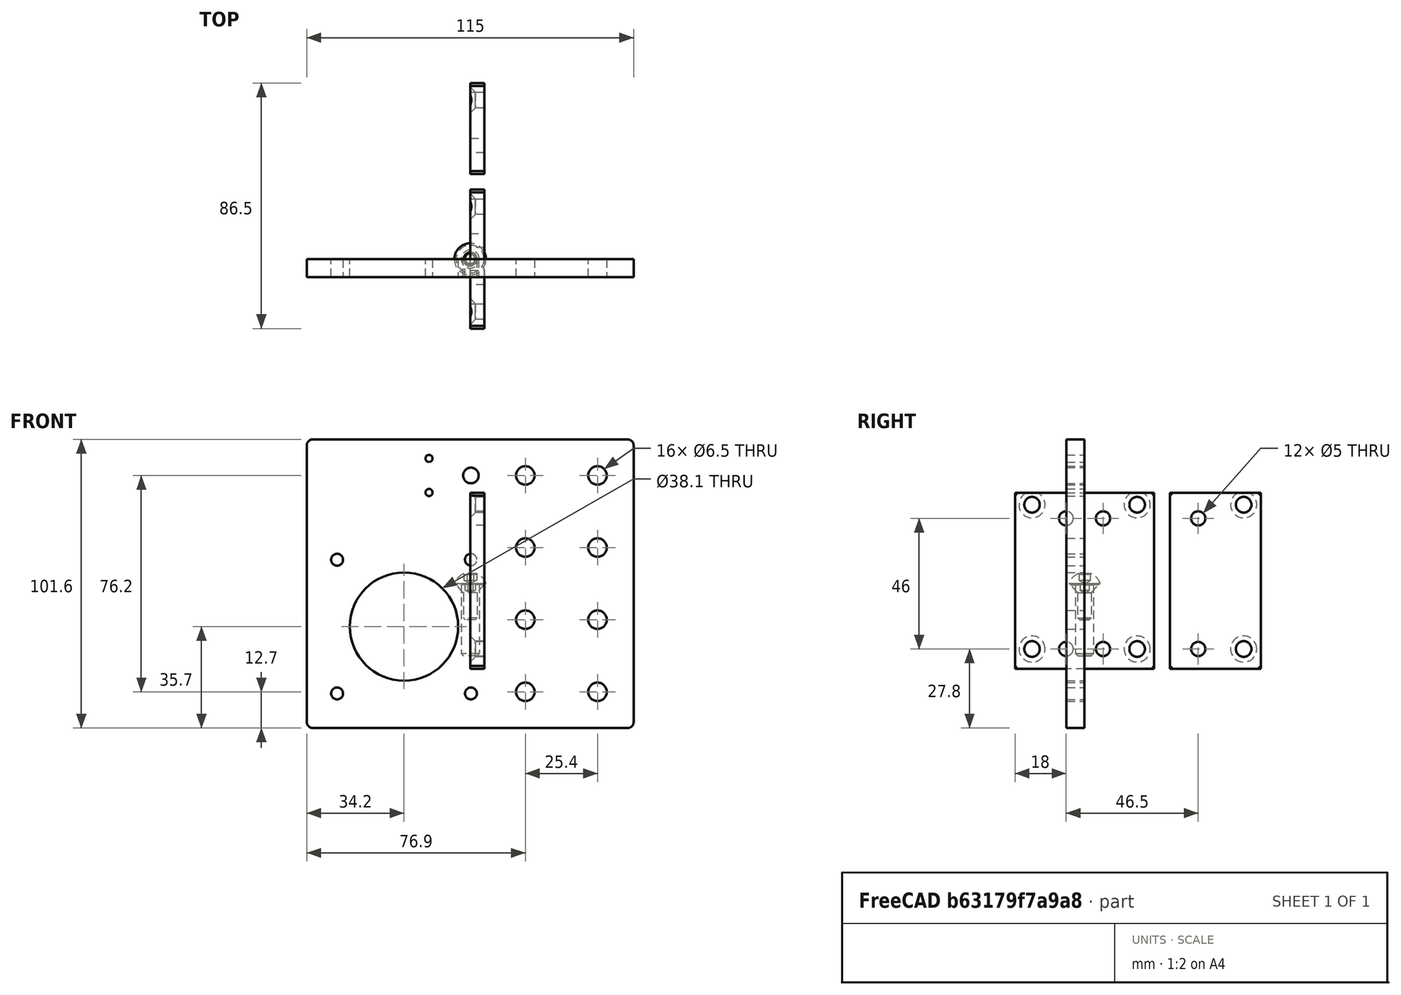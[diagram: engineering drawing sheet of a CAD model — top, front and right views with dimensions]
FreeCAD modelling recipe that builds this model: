
FCSTD DOCUMENT  (FreeCAD 2021.717R24301 +3842 (Git))
Label: Y axis plates
License: Creative Commons Attribution
LicenseURL: http://creativecommons.org/licenses/by/4.0/
objects: App::FeaturePython×164, Part::FeaturePython×120, TechDraw::DrawViewDimension×48, App::LinkElement×44, App::Link×16, PartDesign::Body×8, Sketcher::SketchObject×5, TechDraw::DrawViewPart×5, PartDesign::Pad×4, PartDesign::SubShapeBinder×4, PartDesign::Chamfer×4, PartDesign::Hole×4, TechDraw::DrawSVGTemplate×3, App::DocumentObjectGroup×3, TechDraw::DrawPage×3, PartDesign::Fillet×2, PartDesign::ShapeBinder×1, PartDesign::Pocket×1, TechDraw::DrawViewAnnotation×1
note: 175 computed .brp shape members not serialized (recipe doc carries the construction recipe); baked Part::Feature solids carry a one-line shape summary decoded from their .brp

FEATURE [Sketcher::SketchObject] Sketch
  FullyConstrained = true
  MapMode = 5
  Placement = pos=(0,0,0) rot=(0.57735,0.57735,0.57735;2.0944rad)
  Support = -> [YZ_Plane]
  sketch-geometry (16):
    g0: LineSegment StartX=-24.5 StartY=32 StartZ=0 EndX=24.5 EndY=32 EndZ=0
    g1: LineSegment StartX=24.5 StartY=32 StartZ=0 EndX=24.5 EndY=-30 EndZ=0
    g2: LineSegment StartX=24.5 StartY=-30 StartZ=0 EndX=-24.5 EndY=-30 EndZ=0
    g3: LineSegment StartX=-24.5 StartY=-30 StartZ=0 EndX=-24.5 EndY=32 EndZ=0
    g4: LineSegment [constr] StartX=-12.5 StartY=30 StartZ=0 EndX=12.5 EndY=30 EndZ=0
    g5: LineSegment [constr] StartX=12.5 StartY=30 StartZ=0 EndX=12.5 EndY=-30 EndZ=0
    g6: LineSegment [constr] StartX=12.5 StartY=-30 StartZ=0 EndX=-12.5 EndY=-30 EndZ=0
    g7: LineSegment [constr] StartX=-12.5 StartY=-30 StartZ=0 EndX=-12.5 EndY=30 EndZ=0
    g8: Circle CenterX=-6.5 CenterY=23 CenterZ=0 NormalX=0 NormalY=0 NormalZ=1 AngleXU=0 Radius=2.5
    g9: Circle CenterX=6.5 CenterY=23 CenterZ=0 NormalX=0 NormalY=0 NormalZ=1 AngleXU=0 Radius=2.5
    g10: Circle CenterX=-6.5 CenterY=-23 CenterZ=0 NormalX=0 NormalY=0 NormalZ=1 AngleXU=0 Radius=2.5
    g11: Circle CenterX=6.5 CenterY=-23 CenterZ=0 NormalX=0 NormalY=0 NormalZ=1 AngleXU=0 Radius=2.5
    g12: Circle CenterX=18.5 CenterY=-23 CenterZ=0 NormalX=0 NormalY=0 NormalZ=1 AngleXU=0 Radius=2.75
    g13: Circle CenterX=18.5 CenterY=27.8 CenterZ=0 NormalX=0 NormalY=0 NormalZ=1 AngleXU=0 Radius=2.75
    g14: Circle CenterX=-18.5 CenterY=27.8 CenterZ=0 NormalX=0 NormalY=0 NormalZ=1 AngleXU=0 Radius=2.75
    g15: Circle CenterX=-18.5 CenterY=-23 CenterZ=0 NormalX=0 NormalY=0 NormalZ=1 AngleXU=0 Radius=2.75
  constraints (44):
    c: Coincident(g0,g1)
    c: Coincident(g1,g2)
    c: Coincident(g2,g3)
    c: Coincident(g3,g0)
    c: Horizontal(g0)
    c: Vertical(g1)
    c: Vertical(g3)
    c: Coincident(g4,g5)
    c: Coincident(g5,g6)
    c: Coincident(g6,g7)
    c: Coincident(g7,g4)
    c: Horizontal(g4)
    c: Horizontal(g6)
    c: Vertical(g5)
    c: Vertical(g7)
    c: Symmetric(g5,g4,g-1)
    c: DistanceY(g5,g5) = 60
    c: DistanceX(g4,g4) = 25
    c: Symmetric(g8,g11,g-1)
    c: Vertical(g8,g10)
    c: Vertical(g9,g11)
    c: Horizontal(g8,g9)
    c: Horizontal(g10,g11)
    c: Equal(g8,g9)
    c: Diameter(g9) = 5
    c: DistanceX(g10,g11) = 13
    c: DistanceY(g11,g9) = 46
    c: Horizontal(g2,g6)
    c: DistanceX(g4,g13) = 6
    c: DistanceX(g13,g0) = 6
    c: DistanceY(g12,g13) = 50.8
    c: Equal(g13,g12)
    c: Diameter(g13) = 5.5
    c: Vertical(g12,g13)
    c: Horizontal(g11,g12)
    c: Symmetric(g1,g2,g-2)
    c: Equal(g15,g14)
    c: Equal(g14,g13)
    c: Horizontal(g14,g13)
    c: Symmetric(g12,g15,g-2)
    c: Vertical(g14,g15)
    c: Equal(g10,g11)
    c: Equal(g10,g8)
    c: DistanceY(g3,g3) = 62
FEATURE [PartDesign::Pad] Pad
  ClaimChildren = false
  Direction = (1,1,1)
  Fit = 0
  FitJoin = 0
  InnerFit = 0
  InnerFitJoin = 0
  InnerTaperAngle = 0
  InnerTaperAngleRev = 0
  Length = 5
  Length2 = 100
  Linearize = true
  NewSolid = false
  Placement = pos=(0,0,0) rot=(0.57735,0.57735,0.57735;2.0944rad)
  Profile = -> Sketch
  Refine = true
  Suppress = false
  Type = 0
  _ProfileBasedVersion = 0
FEATURE [PartDesign::Body] Body  label="BK12 plate"
  AutoGroupSolids = false
  ExportMode = 0
  Group = -> [Sketch,Pad]
  Origin = -> Origin
  Tip = -> Pad
  _ExportChildren = -> [Pad]
  _GroupVersion = 1
FEATURE [Sketcher::SketchObject] Sketch001
  FullyConstrained = true
  MapMode = 5
  Placement = pos=(0,0,0) rot=(0.57735,0.57735,0.57735;2.0944rad)
  Support = -> [YZ_Plane001]
  sketch-geometry (12):
    g0: LineSegment [constr] StartX=-10 StartY=30 StartZ=0 EndX=10 EndY=30 EndZ=0
    g1: LineSegment [constr] StartX=10 StartY=30 StartZ=0 EndX=10 EndY=-30 EndZ=0
    g2: LineSegment [constr] StartX=10 StartY=-30 StartZ=0 EndX=-10 EndY=-30 EndZ=0
    g3: LineSegment [constr] StartX=-10 StartY=-30 StartZ=0 EndX=-10 EndY=30 EndZ=0
    g4: Circle CenterX=0 CenterY=23 CenterZ=0 NormalX=0 NormalY=0 NormalZ=1 AngleXU=0 Radius=2.5
    g5: Circle CenterX=0 CenterY=-23 CenterZ=0 NormalX=0 NormalY=0 NormalZ=1 AngleXU=0 Radius=2.5
    g6: Circle CenterX=16 CenterY=27.8 CenterZ=0 NormalX=0 NormalY=0 NormalZ=1 AngleXU=0 Radius=2.75
    g7: Circle CenterX=16 CenterY=-23 CenterZ=0 NormalX=0 NormalY=0 NormalZ=1 AngleXU=0 Radius=2.75
    g8: LineSegment StartX=-10 StartY=-30 StartZ=0 EndX=22 EndY=-30 EndZ=0
    g9: LineSegment StartX=22 StartY=-30 StartZ=0 EndX=22 EndY=32 EndZ=0
    g10: LineSegment StartX=22 StartY=32 StartZ=0 EndX=-10 EndY=32 EndZ=0
    g11: LineSegment StartX=-10 StartY=32 StartZ=0 EndX=-10 EndY=-30 EndZ=0
  constraints (33):
    c: Coincident(g0,g1)
    c: Coincident(g1,g2)
    c: Coincident(g2,g3)
    c: Coincident(g3,g0)
    c: Horizontal(g0)
    c: Horizontal(g2)
    c: Vertical(g1)
    c: Vertical(g3)
    c: Symmetric(g1,g0,g-1)
    c: DistanceX(g0,g0) = 20
    c: DistanceY(g1,g1) = 60
    c: PointOnObject(g4,g-2)
    c: Symmetric(g5,g4,g-1)
    c: DistanceY(g5,g4) = 46
    c: Diameter(g4) = 5
    c: Diameter(g7) = 5.5
    c: Equal(g7,g6)
    c: Horizontal(g7,g5)
    c: Vertical(g7,g6)
    c: DistanceY(g7,g6) = 50.8
    c: DistanceX(g0,g6) = 6
    c: Coincident(g8,g9)
    c: Coincident(g9,g10)
    c: Coincident(g10,g11)
    c: Coincident(g11,g8)
    c: Horizontal(g8)
    c: Horizontal(g10)
    c: Vertical(g9)
    c: Vertical(g11)
    c: Coincident(g8,g2)
    c: DistanceX(g6,g9) = 6
    c: Equal(g5,g4)
    c: DistanceY(g9,g9) = 62
FEATURE [PartDesign::Pad] Pad001
  ClaimChildren = false
  Direction = (1,1,1)
  Fit = 0
  FitJoin = 0
  InnerFit = 0
  InnerFitJoin = 0
  InnerTaperAngle = 0
  InnerTaperAngleRev = 0
  Length = 5
  Length2 = 100
  Linearize = true
  NewSolid = false
  Placement = pos=(0,0,0) rot=(0.57735,0.57735,0.57735;2.0944rad)
  Profile = -> Sketch001
  Refine = true
  Suppress = false
  Type = 0
  _ProfileBasedVersion = 0
FEATURE [PartDesign::Body] Body001  label="BF12 plate"
  AutoGroupSolids = false
  ExportMode = 0
  Group = -> [Sketch001,Pad001]
  Origin = -> Origin001
  Placement = pos=(0,40,0) rot=(0,0,1;0rad)
  Tip = -> Pad001
  _ExportChildren = -> [Pad001]
  _GroupVersion = 1
FEATURE [PartDesign::SubShapeBinder] BaseFeature  label="BaseFeature(BF12 plate)"
  BindCopyOnChange = 0
  BindMode = 0
  ClaimChildren = false
  Context = -> Body002 [BaseFeature.]
  FillStyle = 0
  Fuse = true
  MakeFace = true
  PartialLoad = false
  Relative = true
  Support = -> [Body001]
  _Version = 8
FEATURE [PartDesign::Chamfer] Chamfer
  Angle = 45
  Base = -> BaseFeature [Edge5,Edge8,Edge2,Edge1]
  ChamferType = 0
  FlipDirection = false
  NewSolid = false
  Refine = true
  Size = 1
  Size2 = 1
  SupportTransform = false
  Suppress = false
FEATURE [PartDesign::Hole] Hole
  BaseFeature = -> Chamfer
  ClaimChildren = false
  CustomThreadClearance = 0
  Depth = 25
  DepthType = 0
  Diameter = 5.5
  DrillForDepth = false
  DrillPoint = 1
  DrillPointAngle = 118
  Fit = 0
  FitJoin = 0
  HoleCutCountersinkAngle = 90
  HoleCutCustomValues = false
  HoleCutDepth = 0
  HoleCutDiameter = 9.2
  HoleCutType = 2
  InnerFit = 0
  InnerFitJoin = 0
  ModelThread = false
  NewSolid = false
  Profile = -> Chamfer [Edge26,Edge25]
  Refine = true
  Suppress = false
  Tapered = false
  TaperedAngle = 90
  ThreadClass = 0
  ThreadDepth = 23.5
  ThreadDepthType = 0
  ThreadDirection = 0
  ThreadFit = 0
  ThreadSize = 0
  ThreadType = 0
  Threaded = false
  UseCustomThreadClearance = false
  _ProfileBasedVersion = 0
FEATURE [PartDesign::Body] Body002  label="BF12R plate"
  AutoGroupSolids = false
  BaseFeature = -> BaseFeature
  ExportMode = 0
  Group = -> [BaseFeature,Chamfer,Hole]
  Origin = -> Origin002
  Tip = -> Hole
  _ExportChildren = -> [BaseFeature,Hole]
  _GroupVersion = 1
FEATURE [PartDesign::SubShapeBinder] BaseFeature001  label="BaseFeature001(BF12 plate)"
  BindCopyOnChange = 0
  BindMode = 0
  ClaimChildren = false
  Context = -> Body003 [BaseFeature001.]
  FillStyle = 0
  Fuse = true
  MakeFace = true
  PartialLoad = false
  Relative = true
  Support = -> [Body001]
  _Version = 8
FEATURE [PartDesign::Chamfer] Chamfer001
  Angle = 45
  Base = -> BaseFeature001 [Edge5,Edge8,Edge2,Edge1]
  ChamferType = 0
  FlipDirection = false
  NewSolid = false
  Refine = true
  Size = 1
  Size2 = 1
  SupportTransform = false
  Suppress = false
FEATURE [PartDesign::Hole] Hole001
  BaseFeature = -> Chamfer001
  ClaimChildren = false
  CustomThreadClearance = 0
  Depth = 25
  DepthType = 0
  Diameter = 5.5
  DrillForDepth = false
  DrillPoint = 1
  DrillPointAngle = 118
  Fit = 0
  FitJoin = 0
  HoleCutCountersinkAngle = 90
  HoleCutCustomValues = false
  HoleCutDepth = 0
  HoleCutDiameter = 9.2
  HoleCutType = 2
  InnerFit = 0
  InnerFitJoin = 0
  ModelThread = false
  NewSolid = false
  Profile = -> Chamfer001 [Edge13,Edge12]
  Refine = true
  Reversed = true
  Suppress = false
  Tapered = false
  TaperedAngle = 90
  ThreadClass = 0
  ThreadDepth = 23.5
  ThreadDepthType = 0
  ThreadDirection = 0
  ThreadFit = 0
  ThreadSize = 0
  ThreadType = 0
  Threaded = false
  UseCustomThreadClearance = false
  _ProfileBasedVersion = 0
FEATURE [PartDesign::Body] Body003  label="BF12L plate"
  AutoGroupSolids = false
  BaseFeature = -> BaseFeature001
  ExportMode = 0
  Group = -> [BaseFeature001,Chamfer001,Hole001]
  Origin = -> Origin003
  Tip = -> Hole001
  _ExportChildren = -> [BaseFeature001,Hole001]
  _GroupVersion = 1
FEATURE [PartDesign::SubShapeBinder] BaseFeature002  label="BaseFeature002(BK12 plate)"
  BindCopyOnChange = 0
  BindMode = 0
  ClaimChildren = false
  Context = -> Body004 [BaseFeature002.]
  FillStyle = 0
  Fuse = true
  MakeFace = true
  PartialLoad = false
  Relative = true
  Support = -> [Body]
  _Version = 8
FEATURE [PartDesign::Chamfer] Chamfer002
  Angle = 45
  Base = -> BaseFeature002 [Edge2,Edge1,Edge5,Edge8]
  ChamferType = 0
  FlipDirection = false
  NewSolid = false
  Refine = true
  Size = 1
  Size2 = 1
  SupportTransform = false
  Suppress = false
FEATURE [PartDesign::Hole] Hole002
  BaseFeature = -> Chamfer002
  ClaimChildren = false
  CustomThreadClearance = 0
  Depth = 25
  DepthType = 0
  Diameter = 5.5
  DrillForDepth = false
  DrillPoint = 1
  DrillPointAngle = 118
  Fit = 0
  FitJoin = 0
  HoleCutCountersinkAngle = 90
  HoleCutCustomValues = false
  HoleCutDepth = 0
  HoleCutDiameter = 9.2
  HoleCutType = 2
  InnerFit = 0
  InnerFitJoin = 0
  ModelThread = false
  NewSolid = false
  Profile = -> Chamfer002 [Edge29,Edge32,Edge31,Edge30]
  Refine = true
  Suppress = false
  Tapered = false
  TaperedAngle = 90
  ThreadClass = 0
  ThreadDepth = 23.5
  ThreadDepthType = 0
  ThreadDirection = 0
  ThreadFit = 0
  ThreadSize = 0
  ThreadType = 0
  Threaded = false
  UseCustomThreadClearance = false
  _ProfileBasedVersion = 0
FEATURE [PartDesign::Body] Body004  label="BK12R plate"
  AutoGroupSolids = false
  BaseFeature = -> BaseFeature002
  ExportMode = 0
  Group = -> [BaseFeature002,Chamfer002,Hole002]
  Origin = -> Origin004
  Tip = -> Hole002
  _ExportChildren = -> [BaseFeature002,Hole002]
  _GroupVersion = 1
FEATURE [PartDesign::SubShapeBinder] BaseFeature003  label="BaseFeature003(BK12 plate)"
  BindCopyOnChange = 0
  BindMode = 0
  ClaimChildren = false
  Context = -> Body005 [BaseFeature003.]
  FillStyle = 0
  Fuse = true
  MakeFace = true
  PartialLoad = false
  Relative = true
  Support = -> [Body]
  _Version = 8
FEATURE [PartDesign::Chamfer] Chamfer003
  Angle = 45
  Base = -> BaseFeature003 [Edge2,Edge1,Edge8,Edge5]
  ChamferType = 0
  FlipDirection = false
  NewSolid = false
  Refine = true
  Size = 1
  Size2 = 1
  SupportTransform = false
  Suppress = false
FEATURE [PartDesign::Hole] Hole003
  BaseFeature = -> Chamfer003
  ClaimChildren = false
  CustomThreadClearance = 0
  Depth = 25
  DepthType = 0
  Diameter = 5.5
  DrillForDepth = false
  DrillPoint = 1
  DrillPointAngle = 118
  Fit = 0
  FitJoin = 0
  HoleCutCountersinkAngle = 90
  HoleCutCustomValues = false
  HoleCutDepth = 0
  HoleCutDiameter = 9.2
  HoleCutType = 2
  InnerFit = 0
  InnerFitJoin = 0
  ModelThread = false
  NewSolid = false
  Profile = -> Chamfer003 [Edge12,Edge15,Edge14,Edge13]
  Refine = true
  Reversed = true
  Suppress = false
  Tapered = false
  TaperedAngle = 90
  ThreadClass = 0
  ThreadDepth = 23.5
  ThreadDepthType = 0
  ThreadDirection = 0
  ThreadFit = 0
  ThreadSize = 0
  ThreadType = 0
  Threaded = false
  UseCustomThreadClearance = false
  _ProfileBasedVersion = 0
FEATURE [PartDesign::Body] Body005  label="BK12L plate"
  AutoGroupSolids = false
  BaseFeature = -> BaseFeature003
  ExportMode = 0
  Group = -> [BaseFeature003,Chamfer003,Hole003]
  Origin = -> Origin005
  Tip = -> Hole003
  _ExportChildren = -> [BaseFeature003,Hole003]
  _GroupVersion = 1
FEATURE [App::Link] Link  label="Link(BK12R plate)"
  AutoLinkLabel = true
  AutoPlacement = true
  LinkedObject = -> Body004
  SyncGroupVisibility = false
  _LinkVersion = 1
FEATURE [App::Link] Link001  label="Link001(BK12L plate)"
  AutoLinkLabel = true
  AutoPlacement = true
  LinkedObject = -> Body005
  SyncGroupVisibility = false
  _LinkVersion = 1
FEATURE [App::Link] Link002  label="Link002(BF12L plate)"
  AutoLinkLabel = true
  AutoPlacement = true
  LinkedObject = -> Body003
  SyncGroupVisibility = false
  _LinkVersion = 1
FEATURE [App::Link] Link003  label="Link003(BF12R plate)"
  AutoLinkLabel = true
  AutoPlacement = true
  LinkedObject = -> Body002
  SyncGroupVisibility = false
  _LinkVersion = 1
FEATURE [Sketcher::SketchObject] Sketch002
  FullyConstrained = true
  MapMode = 5
  Placement = pos=(0,0,0) rot=(1,0,0;1.5708rad)
  Support = -> [XZ_Plane006]
  sketch-geometry (23):
    g0: LineSegment StartX=-57.5 StartY=50.8 StartZ=0 EndX=57.5 EndY=50.8 EndZ=0
    g1: LineSegment StartX=57.5 StartY=50.8 StartZ=0 EndX=57.5 EndY=-50.8 EndZ=0
    g2: LineSegment StartX=57.5 StartY=-50.8 StartZ=0 EndX=-57.5 EndY=-50.8 EndZ=0
    g3: LineSegment StartX=-57.5 StartY=-50.8 StartZ=0 EndX=-57.5 EndY=50.8 EndZ=0
    g4: Circle CenterX=19.4 CenterY=38.1 CenterZ=0 NormalX=0 NormalY=0 NormalZ=1 AngleXU=0 Radius=3.25
    g5: Circle CenterX=44.8 CenterY=38.1 CenterZ=0 NormalX=0 NormalY=0 NormalZ=1 AngleXU=0 Radius=3.25
    g6: Circle CenterX=19.4 CenterY=12.7 CenterZ=0 NormalX=0 NormalY=0 NormalZ=1 AngleXU=0 Radius=3.25
    g7: Circle CenterX=44.8 CenterY=12.7 CenterZ=0 NormalX=0 NormalY=0 NormalZ=1 AngleXU=0 Radius=3.25
    g8: Circle CenterX=19.4 CenterY=-12.7 CenterZ=0 NormalX=0 NormalY=0 NormalZ=1 AngleXU=0 Radius=3.25
    g9: Circle CenterX=44.8 CenterY=-12.7 CenterZ=0 NormalX=0 NormalY=0 NormalZ=1 AngleXU=0 Radius=3.25
    g10: Circle CenterX=19.4 CenterY=-38.1 CenterZ=0 NormalX=0 NormalY=0 NormalZ=1 AngleXU=0 Radius=3.25
    g11: Circle CenterX=44.8 CenterY=-38.1 CenterZ=0 NormalX=0 NormalY=0 NormalZ=1 AngleXU=0 Radius=3.25
    g12: LineSegment [constr] StartX=19.4 StartY=38.1 StartZ=0 EndX=44.8 EndY=38.1 EndZ=0
    g13: LineSegment [constr] StartX=19.4 StartY=38.1 StartZ=0 EndX=19.4 EndY=12.7 EndZ=0
    g14: LineSegment [constr] StartX=19.4 StartY=12.7 StartZ=0 EndX=19.4 EndY=-12.7 EndZ=0
    g15: LineSegment [constr] StartX=19.4 StartY=-12.7 StartZ=0 EndX=19.4 EndY=-38.1 EndZ=0
    g16: Circle CenterX=-23.3 CenterY=-15.1 CenterZ=0 NormalX=0 NormalY=0 NormalZ=1 AngleXU=0 Radius=19.05
    g17: Circle CenterX=-46.85 CenterY=8.45 CenterZ=0 NormalX=0 NormalY=0 NormalZ=1 AngleXU=0 Radius=2.1
    g18: Circle CenterX=0.25 CenterY=8.45 CenterZ=0 NormalX=0 NormalY=0 NormalZ=1 AngleXU=0 Radius=2.1
    g19: Circle CenterX=-46.85 CenterY=-38.65 CenterZ=0 NormalX=0 NormalY=0 NormalZ=1 AngleXU=0 Radius=2.1
    g20: Circle CenterX=0.25 CenterY=-38.65 CenterZ=0 NormalX=0 NormalY=0 NormalZ=1 AngleXU=0 Radius=2.1
    g21: LineSegment [constr] StartX=-46.85 StartY=8.45 StartZ=0 EndX=0.25 EndY=8.45 EndZ=0
    g22: LineSegment [constr] StartX=-46.85 StartY=8.45 StartZ=0 EndX=-46.85 EndY=-38.65 EndZ=0
  constraints (56):
    c: Coincident(g0,g1)
    c: Coincident(g1,g2)
    c: Coincident(g2,g3)
    c: Coincident(g3,g0)
    c: Horizontal(g0)
    c: Horizontal(g2)
    c: Vertical(g1)
    c: Vertical(g3)
    c: DistanceX(g0,g0) = 115
    c: DistanceY(g1,g1) = 101.6
    c: Symmetric(g2,g0,g-1)
    c: Diameter(g4) = 6.5
    c: Equal(g4, g5-g9) x5
    c: Equal(g4,g11)
    c: Equal(g4,g10)
    c: Vertical(g4,g6)
    c: Vertical(g8,g10)
    c: Vertical(g5,g7)
    c: Vertical(g7,g9)
    c: Vertical(g9,g11)
    c: Horizontal(g10,g11)
    c: Horizontal(g4,g5)
    c: Horizontal(g6,g7)
    c: Horizontal(g8,g9)
    c: DistanceX(g5,g0) = 12.7
    c: Coincident(g12,g4)
    c: Coincident(g12,g5)
    c: Coincident(g13,g4)
    c: Coincident(g13,g6)
    c: Coincident(g14,g6)
    c: Coincident(g14,g8)
    c: Coincident(g15,g8)
    c: Coincident(g15,g10)
    c: Equal(g15,g14)
    c: Equal(g14,g13)
    c: Equal(g13,g12)
    c: DistanceX(g10,g11) = 25.4
    c: Symmetric(g6,g8,g-1)
    c: Horizontal(g20,g19)
    c: Horizontal(g17,g18)
    c: Vertical(g18,g20)
    c: Vertical(g17,g19)
    c: Diameter(g19) = 4.2
    c: Equal(g19,g20)
    c: Equal(g19,g18)
    c: Equal(g19,g17)
    c: Symmetric(g19,g18,g16)
    c: Diameter(g16) = 38.1
    c: Coincident(g21,g17)
    c: Coincident(g21,g18)
    c: Coincident(g22,g17)
    c: Coincident(g22,g19)
    c: Equal(g22,g21)
    c: DistanceX(g21,g21) = 47.1
    c: DistanceY(g10,g16) = 23
    c: DistanceX(g16,g10) = 42.7
FEATURE [PartDesign::Pad] Pad002
  ClaimChildren = false
  Direction = (1,1,1)
  Fit = 0
  FitJoin = 0
  InnerFit = 0
  InnerFitJoin = 0
  InnerTaperAngle = 0
  InnerTaperAngleRev = 0
  Length = 6.35
  Length2 = 100
  Linearize = true
  NewSolid = false
  Placement = pos=(0,0,0) rot=(1,0,0;1.5708rad)
  Profile = -> Sketch002
  Refine = true
  Suppress = false
  Type = 0
  _ProfileBasedVersion = 0
FEATURE [PartDesign::Fillet] Fillet
  Base = -> Pad002 [Edge2,Edge5,Edge8,Edge1]
  BaseFeature = -> Pad002
  NewSolid = false
  Placement = pos=(0,0,0) rot=(1,0,0;1.5708rad)
  Radius = 2
  Refine = true
  SupportTransform = false
  Suppress = false
FEATURE [App::Link] Link004  label="Link004(motor plate)"
  AutoLinkLabel = true
  AutoPlacement = true
  LinkedObject = -> Body006
  SyncGroupVisibility = false
  _LinkVersion = 1
FEATURE [App::Link] Link006  label="Link006(motor plate)"
  AutoLinkLabel = true
  AutoPlacement = true
  LinkPlacement = pos=(-2.99056e-05,-7,0) rot=(0,0,1;3.14159rad)
  LinkedObject = -> Body006
  Placement = pos=(-2.99056e-05,-7,0) rot=(0,0,1;3.14159rad)
  SyncGroupVisibility = false
  _LinkVersion = 1
FEATURE [Part::FeaturePython] Screw  label="1/4inx1in-Screw"  # Fasteners workbench fastener (typed FeaturePython)
  diameter = 11
  invert = false
  length = 6
  lengthCustom = 25.4
  matchOuter = false
  offset = 0
  thread = false
  type = 4
FEATURE [App::LinkElement] Link007_i0
  LinkPlacement = pos=(19.4,32.65,38.1) rot=(1,0,0;1.5708rad)
  LinkedObject = -> Screw
  Placement = pos=(19.4,32.65,38.1) rot=(1,0,0;1.5708rad)
  _LinkVersion = 1
FEATURE [App::LinkElement] Link007_i1
  LinkPlacement = pos=(44.8,32.65,38.1) rot=(1,0,0;1.5708rad)
  LinkedObject = -> Screw
  Placement = pos=(44.8,32.65,38.1) rot=(1,0,0;1.5708rad)
  _LinkVersion = 1
FEATURE [App::LinkElement] Link007_i2
  LinkPlacement = pos=(19.4,32.65,12.7) rot=(1,0,0;1.5708rad)
  LinkedObject = -> Screw
  Placement = pos=(19.4,32.65,12.7) rot=(1,0,0;1.5708rad)
  _LinkVersion = 1
FEATURE [App::LinkElement] Link007_i3
  LinkPlacement = pos=(44.8,32.65,12.7) rot=(1,0,0;1.5708rad)
  LinkedObject = -> Screw
  Placement = pos=(44.8,32.65,12.7) rot=(1,0,0;1.5708rad)
  _LinkVersion = 1
FEATURE [App::LinkElement] Link007_i4
  LinkPlacement = pos=(44.8,32.65,-12.7) rot=(1,0,0;1.5708rad)
  LinkedObject = -> Screw
  Placement = pos=(44.8,32.65,-12.7) rot=(1,0,0;1.5708rad)
  _LinkVersion = 1
FEATURE [App::LinkElement] Link007_i5
  LinkPlacement = pos=(19.4,32.65,-12.7) rot=(1,0,0;1.5708rad)
  LinkedObject = -> Screw
  Placement = pos=(19.4,32.65,-12.7) rot=(1,0,0;1.5708rad)
  _LinkVersion = 1
FEATURE [App::LinkElement] Link007_i6
  LinkPlacement = pos=(44.8,32.65,-38.1) rot=(1,0,0;1.5708rad)
  LinkedObject = -> Screw
  Placement = pos=(44.8,32.65,-38.1) rot=(1,0,0;1.5708rad)
  _LinkVersion = 1
FEATURE [App::LinkElement] Link007_i7
  LinkPlacement = pos=(19.4,32.65,-38.1) rot=(1,0,0;1.5708rad)
  LinkedObject = -> Screw
  Placement = pos=(19.4,32.65,-38.1) rot=(1,0,0;1.5708rad)
  _LinkVersion = 1
FEATURE [App::Link] Link007  label="1/4inx1in-Screw 8ct"
  AutoLinkLabel = true
  AutoPlacement = true
  ElementCount = 8
  ElementList = -> [Link007_i0,Link007_i1,Link007_i2,Link007_i3,Link007_i4,Link007_i5,Link007_i6,Link007_i7]
  LinkPlacement = pos=(0,-39,0) rot=(0,0,1;0rad)
  LinkedObject = -> Screw
  Placement = pos=(0,-39,0) rot=(0,0,1;0rad)
  SyncGroupVisibility = false
  _LinkVersion = 1
FEATURE [Part::FeaturePython] Parts004  # WARN: FeaturePython — macro-defined, semantics opaque (R4)
  Group = -> [Link004,Link007]
  GroupMode = 0
  _LinkVersion = 1
FEATURE [App::LinkElement] Link008_i0
  LinkPlacement = pos=(-44.8,17,38.1) rot=(0,-0.707107,0.707107;3.14159rad)
  LinkedObject = -> Screw
  Placement = pos=(-44.8,17,38.1) rot=(0,-0.707107,0.707107;3.14159rad)
  _LinkVersion = 1
FEATURE [App::LinkElement] Link008_i1
  LinkPlacement = pos=(-19.4,17,38.1) rot=(0,-0.707107,0.707107;3.14159rad)
  LinkedObject = -> Screw
  Placement = pos=(-19.4,17,38.1) rot=(0,-0.707107,0.707107;3.14159rad)
  _LinkVersion = 1
FEATURE [App::LinkElement] Link008_i2
  LinkPlacement = pos=(-19.4,17,12.7) rot=(0,-0.707107,0.707107;3.14159rad)
  LinkedObject = -> Screw
  Placement = pos=(-19.4,17,12.7) rot=(0,-0.707107,0.707107;3.14159rad)
  _LinkVersion = 1
FEATURE [App::LinkElement] Link008_i3
  LinkPlacement = pos=(-44.8,17,12.7) rot=(0,-0.707107,0.707107;3.14159rad)
  LinkedObject = -> Screw
  Placement = pos=(-44.8,17,12.7) rot=(0,-0.707107,0.707107;3.14159rad)
  _LinkVersion = 1
FEATURE [App::LinkElement] Link008_i4
  LinkPlacement = pos=(-19.4,17,-12.7) rot=(0,-0.707107,0.707107;3.14159rad)
  LinkedObject = -> Screw
  Placement = pos=(-19.4,17,-12.7) rot=(0,-0.707107,0.707107;3.14159rad)
  _LinkVersion = 1
FEATURE [App::LinkElement] Link008_i5
  LinkPlacement = pos=(-44.8,17,-12.7) rot=(0,-0.707107,0.707107;3.14159rad)
  LinkedObject = -> Screw
  Placement = pos=(-44.8,17,-12.7) rot=(0,-0.707107,0.707107;3.14159rad)
  _LinkVersion = 1
FEATURE [App::LinkElement] Link008_i6
  LinkPlacement = pos=(-19.4,17,-38.1) rot=(0,-0.707107,0.707107;3.14159rad)
  LinkedObject = -> Screw
  Placement = pos=(-19.4,17,-38.1) rot=(0,-0.707107,0.707107;3.14159rad)
  _LinkVersion = 1
FEATURE [App::LinkElement] Link008_i7
  LinkPlacement = pos=(-44.8,17,-38.1) rot=(0,-0.707107,0.707107;3.14159rad)
  LinkedObject = -> Screw
  Placement = pos=(-44.8,17,-38.1) rot=(0,-0.707107,0.707107;3.14159rad)
  _LinkVersion = 1
FEATURE [App::Link] Link008  label="1/4inx1in-Screw 8ct "
  AutoLinkLabel = true
  AutoPlacement = true
  ElementCount = 8
  ElementList = -> [Link008_i0,Link008_i1,Link008_i2,Link008_i3,Link008_i4,Link008_i5,Link008_i6,Link008_i7]
  LinkPlacement = pos=(0,-24,0) rot=(0,0,1;0rad)
  LinkedObject = -> Screw
  Placement = pos=(0,-24,0) rot=(0,0,1;0rad)
  SyncGroupVisibility = false
  _LinkVersion = 1
FEATURE [Part::FeaturePython] Parts005  # WARN: FeaturePython — macro-defined, semantics opaque (R4)
  Group = -> [Link006,Link008]
  GroupMode = 0
  _LinkVersion = 1
FEATURE [Part::FeaturePython] Screw001  label="#10x1/2in-Screw"  # Fasteners workbench fastener (typed FeaturePython)
  diameter = 9
  invert = false
  length = 4
  lengthCustom = 12.7
  matchOuter = false
  offset = 0
  thread = false
  type = 3
FEATURE [App::LinkElement] Link009_i0
  LinkPlacement = pos=(0,2.13e-14,-1.99e-14) rot=(0,0,1;0rad)
  LinkedObject = -> Screw001
  Placement = pos=(0,2.13e-14,-1.99e-14) rot=(0,0,1;0rad)
  _LinkVersion = 1
FEATURE [App::LinkElement] Link009_i1
  LinkPlacement = pos=(-50.8,2.84e-14,-1.6e-15) rot=(0,0,1;0rad)
  LinkedObject = -> Screw001
  Placement = pos=(-50.8,2.84e-14,-1.6e-15) rot=(0,0,1;0rad)
  _LinkVersion = 1
FEATURE [App::Link] Link009  label="#10x3/8in-Screw 2ct"
  AutoLinkLabel = true
  AutoPlacement = true
  ElementCount = 2
  ElementList = -> [Link009_i0,Link009_i1]
  LinkPlacement = pos=(-2.02e-14,56,27.8) rot=(0,-1,0;1.5708rad)
  LinkedObject = -> Screw001
  Placement = pos=(-2.02e-14,56,27.8) rot=(0,-1,0;1.5708rad)
  SyncGroupVisibility = false
  _LinkVersion = 1
FEATURE [Part::FeaturePython] Parts002  # WARN: FeaturePython — macro-defined, semantics opaque (R4)
  Group = -> [Link002,Link009]
  GroupMode = 0
  _LinkVersion = 1
FEATURE [App::LinkElement] Link010_i0
  LinkPlacement = pos=(46.5,-10,27.8) rot=(-0.57735,-0.57735,-0.57735;2.0944rad)
  LinkedObject = -> Screw001
  Placement = pos=(46.5,-10,27.8) rot=(-0.57735,-0.57735,-0.57735;2.0944rad)
  _LinkVersion = 1
FEATURE [App::LinkElement] Link010_i1
  LinkPlacement = pos=(9.5,-10,-23) rot=(-0.57735,-0.57735,-0.57735;2.0944rad)
  LinkedObject = -> Screw001
  Placement = pos=(9.5,-10,-23) rot=(-0.57735,-0.57735,-0.57735;2.0944rad)
  _LinkVersion = 1
FEATURE [App::LinkElement] Link010_i2
  LinkPlacement = pos=(9.5,-10,27.8) rot=(-0.57735,-0.57735,-0.57735;2.0944rad)
  LinkedObject = -> Screw001
  Placement = pos=(9.5,-10,27.8) rot=(-0.57735,-0.57735,-0.57735;2.0944rad)
  _LinkVersion = 1
FEATURE [App::LinkElement] Link010_i3
  LinkPlacement = pos=(46.5,-10,-23) rot=(-0.57735,-0.57735,-0.57735;2.0944rad)
  LinkedObject = -> Screw001
  Placement = pos=(46.5,-10,-23) rot=(-0.57735,-0.57735,-0.57735;2.0944rad)
  _LinkVersion = 1
FEATURE [App::Link] Link010  label="#10x3/8in-Screw 4ct"
  AutoLinkLabel = true
  AutoPlacement = true
  ElementCount = 4
  ElementList = -> [Link010_i0,Link010_i1,Link010_i2,Link010_i3]
  LinkPlacement = pos=(-10,-28,0) rot=(0,0,1;1.5708rad)
  LinkedObject = -> Screw001
  Placement = pos=(-10,-28,0) rot=(0,0,1;1.5708rad)
  SyncGroupVisibility = false
  _LinkVersion = 1
FEATURE [Part::FeaturePython] Parts001  # WARN: FeaturePython — macro-defined, semantics opaque (R4)
  Group = -> [Link001,Link010]
  GroupMode = 0
  _LinkVersion = 1
FEATURE [App::LinkElement] Link011_i0
  LinkPlacement = pos=(-9,56,27.8) rot=(0,1,0;1.5708rad)
  LinkedObject = -> Screw001
  Placement = pos=(-9,56,27.8) rot=(0,1,0;1.5708rad)
  _LinkVersion = 1
FEATURE [App::LinkElement] Link011_i1
  LinkPlacement = pos=(-9,56,-23) rot=(0,1,0;1.5708rad)
  LinkedObject = -> Screw001
  Placement = pos=(-9,56,-23) rot=(0,1,0;1.5708rad)
  _LinkVersion = 1
FEATURE [App::Link] Link011  label="#10x3/8in-Screw 2ct "
  AutoLinkLabel = true
  AutoPlacement = true
  ElementCount = 2
  ElementList = -> [Link011_i0,Link011_i1]
  LinkPlacement = pos=(14,-1.66893e-06,0) rot=(0,0,1;0rad)
  LinkedObject = -> Screw001
  Placement = pos=(14,-1.66893e-06,0) rot=(0,0,1;0rad)
  SyncGroupVisibility = false
  _LinkVersion = 1
FEATURE [Part::FeaturePython] Parts003  # WARN: FeaturePython — macro-defined, semantics opaque (R4)
  Group = -> [Link003,Link011]
  GroupMode = 0
  _LinkVersion = 1
FEATURE [App::LinkElement] Link012_i0
  LinkPlacement = pos=(-20,18.5,-23) rot=(0,1,0;1.5708rad)
  LinkedObject = -> Screw001
  Placement = pos=(-20,18.5,-23) rot=(0,1,0;1.5708rad)
  _LinkVersion = 1
FEATURE [App::LinkElement] Link012_i1
  LinkPlacement = pos=(-20,-18.5,27.8) rot=(0,1,0;1.5708rad)
  LinkedObject = -> Screw001
  Placement = pos=(-20,-18.5,27.8) rot=(0,1,0;1.5708rad)
  _LinkVersion = 1
FEATURE [App::LinkElement] Link012_i2
  LinkPlacement = pos=(-20,-18.5,-23) rot=(0,1,0;1.5708rad)
  LinkedObject = -> Screw001
  Placement = pos=(-20,-18.5,-23) rot=(0,1,0;1.5708rad)
  _LinkVersion = 1
FEATURE [App::LinkElement] Link012_i3
  LinkPlacement = pos=(-20,18.5,27.8) rot=(0,1,0;1.5708rad)
  LinkedObject = -> Screw001
  Placement = pos=(-20,18.5,27.8) rot=(0,1,0;1.5708rad)
  _LinkVersion = 1
FEATURE [App::Link] Link012  label="#10x3/8in-Screw 4ct "
  AutoLinkLabel = true
  AutoPlacement = true
  ElementCount = 4
  ElementList = -> [Link012_i0,Link012_i1,Link012_i2,Link012_i3]
  LinkPlacement = pos=(25,-2.98023e-06,0) rot=(0,0,1;0rad)
  LinkedObject = -> Screw001
  Placement = pos=(25,-2.98023e-06,0) rot=(0,0,1;0rad)
  SyncGroupVisibility = false
  _LinkVersion = 1
FEATURE [Part::FeaturePython] Parts  # WARN: FeaturePython — macro-defined, semantics opaque (R4)
  Group = -> [Link,Link012]
  GroupMode = 0
  _LinkVersion = 1
FEATURE [PartDesign::ShapeBinder] ShapeBinder
  Placement = pos=(0,-6.35,-1.4e-15) rot=(0,0,1;0rad)
  Support = -> [Fillet]
  TraceSupport = false
FEATURE [Sketcher::SketchObject] Sketch003
  ExternalGeometry = -> [ShapeBinder]
  FullyConstrained = true
  MapMode = 5
  Placement = pos=(0,0,0) rot=(1,0,0;1.5708rad)
  Support = -> [XZ_Plane007]
  sketch-geometry (12):
    g0: LineSegment StartX=-57.5 StartY=50.8 StartZ=0 EndX=57.5 EndY=50.8 EndZ=0
    g1: LineSegment StartX=57.5 StartY=50.8 StartZ=0 EndX=57.5 EndY=-50.8 EndZ=0
    g2: LineSegment StartX=57.5 StartY=-50.8 StartZ=0 EndX=-57.5 EndY=-50.8 EndZ=0
    g3: LineSegment StartX=-57.5 StartY=-50.8 StartZ=0 EndX=-57.5 EndY=50.8 EndZ=0
    g4: Circle CenterX=19.4 CenterY=12.7 CenterZ=0 NormalX=0 NormalY=0 NormalZ=1 AngleXU=0 Radius=3.25
    g5: Circle CenterX=44.8 CenterY=12.7 CenterZ=0 NormalX=0 NormalY=0 NormalZ=1 AngleXU=0 Radius=3.25
    g6: Circle CenterX=44.8 CenterY=38.1 CenterZ=0 NormalX=0 NormalY=0 NormalZ=1 AngleXU=0 Radius=3.25
    g7: Circle CenterX=19.4 CenterY=38.1 CenterZ=0 NormalX=0 NormalY=0 NormalZ=1 AngleXU=0 Radius=3.25
    g8: Circle CenterX=19.4 CenterY=-38.1 CenterZ=0 NormalX=0 NormalY=0 NormalZ=1 AngleXU=0 Radius=3.25
    g9: Circle CenterX=19.4 CenterY=-12.7 CenterZ=0 NormalX=0 NormalY=0 NormalZ=1 AngleXU=0 Radius=3.25
    g10: Circle CenterX=44.8 CenterY=-12.7 CenterZ=0 NormalX=0 NormalY=0 NormalZ=1 AngleXU=0 Radius=3.25
    g11: Circle CenterX=44.8 CenterY=-38.1 CenterZ=0 NormalX=0 NormalY=0 NormalZ=1 AngleXU=0 Radius=3.25
  constraints (30):
    c: Coincident(g0,g1)
    c: Coincident(g1,g2)
    c: Coincident(g2,g3)
    c: Coincident(g3,g0)
    c: Horizontal(g0)
    c: Horizontal(g2)
    c: Vertical(g1)
    c: Vertical(g3)
    c: Horizontal(g0,g-3)
    c: Vertical(g0,g-4)
    c: Symmetric(g0,g1,g-1)
    c: Coincident(g4,g-6)
    c: Coincident(g5,g-7)
    c: Coincident(g6,g-8)
    c: Vertical(g11,g10)
    c: Vertical(g10,g6)
    c: Vertical(g4,g7)
    c: Horizontal(g7,g6)
    c: Horizontal(g8,g11)
    c: Horizontal(g9,g10)
    c: Symmetric(g9,g4,g-1)
    c: Symmetric(g7,g8,g-1)
    c: Equal(g4,g5)
    c: Equal(g5,g7)
    c: Equal(g7,g6)
    c: Equal(g6,g8)
    c: Equal(g8,g11)
    c: Equal(g11,g9)
    c: Equal(g9,g10)
    c: Equal(g4,g-6)
FEATURE [PartDesign::Pad] Pad003
  ClaimChildren = false
  Direction = (1,1,1)
  Fit = 0
  FitJoin = 0
  InnerFit = 0
  InnerFitJoin = 0
  InnerTaperAngle = 0
  InnerTaperAngleRev = 0
  Length = 6.35
  Length2 = 100
  Linearize = true
  NewSolid = false
  Placement = pos=(0,0,0) rot=(1,0,0;1.5708rad)
  Profile = -> Sketch003
  Refine = true
  Suppress = false
  Type = 0
  _ProfileBasedVersion = 1
FEATURE [PartDesign::Fillet] Fillet001
  Base = -> Pad003 [Edge1,Edge2,Edge5,Edge8]
  BaseFeature = -> Pad003
  NewSolid = false
  Placement = pos=(0,0,0) rot=(1,0,0;1.5708rad)
  Radius = 2
  Refine = true
  SupportTransform = false
  Suppress = false
FEATURE [PartDesign::Body] Body007  label="front plate"
  AutoGroupSolids = false
  ExportMode = 0
  Group = -> [ShapeBinder,Sketch003,Pad003,Fillet001]
  Origin = -> Origin007
  Tip = -> Fillet001
  _ExportChildren = -> [ShapeBinder,Pad003,Fillet001]
  _GroupVersion = 1
FEATURE [App::Link] Link013  label="Link013(front plate)"
  AutoLinkLabel = true
  AutoPlacement = true
  LinkedObject = -> Body007
  SyncGroupVisibility = false
  _LinkVersion = 1
FEATURE [App::Link] Link014  label="Link014(front plate)"
  AutoLinkLabel = true
  AutoPlacement = true
  LinkedObject = -> Body007
  SyncGroupVisibility = false
  _LinkVersion = 1
FEATURE [App::LinkElement] Link016_i0
  LinkPlacement = pos=(122.8,37.65,12.7) rot=(1,0,0;1.5708rad)
  LinkedObject = -> Screw
  Placement = pos=(122.8,37.65,12.7) rot=(1,0,0;1.5708rad)
  _LinkVersion = 1
FEATURE [App::LinkElement] Link016_i1
  LinkPlacement = pos=(97.4,37.65,12.7) rot=(1,0,0;1.5708rad)
  LinkedObject = -> Screw
  Placement = pos=(97.4,37.65,12.7) rot=(1,0,0;1.5708rad)
  _LinkVersion = 1
FEATURE [App::LinkElement] Link016_i2
  LinkPlacement = pos=(97.4,37.65,38.1) rot=(1,0,0;1.5708rad)
  LinkedObject = -> Screw
  Placement = pos=(97.4,37.65,38.1) rot=(1,0,0;1.5708rad)
  _LinkVersion = 1
FEATURE [App::LinkElement] Link016_i3
  LinkPlacement = pos=(122.8,37.65,38.1) rot=(1,0,0;1.5708rad)
  LinkedObject = -> Screw
  Placement = pos=(122.8,37.65,38.1) rot=(1,0,0;1.5708rad)
  _LinkVersion = 1
FEATURE [App::LinkElement] Link016_i4
  LinkPlacement = pos=(97.4,37.65,-38.1) rot=(1,0,0;1.5708rad)
  LinkedObject = -> Screw
  Placement = pos=(97.4,37.65,-38.1) rot=(1,0,0;1.5708rad)
  _LinkVersion = 1
FEATURE [App::LinkElement] Link016_i5
  LinkPlacement = pos=(122.8,37.65,-38.1) rot=(1,0,0;1.5708rad)
  LinkedObject = -> Screw
  Placement = pos=(122.8,37.65,-38.1) rot=(1,0,0;1.5708rad)
  _LinkVersion = 1
FEATURE [App::LinkElement] Link016_i6
  LinkPlacement = pos=(97.4,37.65,-12.7) rot=(1,0,0;1.5708rad)
  LinkedObject = -> Screw
  Placement = pos=(97.4,37.65,-12.7) rot=(1,0,0;1.5708rad)
  _LinkVersion = 1
FEATURE [App::LinkElement] Link016_i7
  LinkPlacement = pos=(122.8,37.65,-12.7) rot=(1,0,0;1.5708rad)
  LinkedObject = -> Screw
  Placement = pos=(122.8,37.65,-12.7) rot=(1,0,0;1.5708rad)
  _LinkVersion = 1
FEATURE [App::Link] Link016  label="1/4inx1in-Screw 8ct    "
  AutoLinkLabel = true
  AutoPlacement = true
  ElementCount = 8
  ElementList = -> [Link016_i0,Link016_i1,Link016_i2,Link016_i3,Link016_i4,Link016_i5,Link016_i6,Link016_i7]
  LinkPlacement = pos=(-78,-44,0) rot=(0,0,1;0rad)
  LinkedObject = -> Screw
  Placement = pos=(-78,-44,0) rot=(0,0,1;0rad)
  SyncGroupVisibility = false
  _LinkVersion = 1
FEATURE [Part::FeaturePython] Parts006  # WARN: FeaturePython — macro-defined, semantics opaque (R4)
  Group = -> [Link014,Link016]
  GroupMode = 0
  _LinkVersion = 1
FEATURE [App::LinkElement] Link015_i0
  LinkPlacement = pos=(191.8,-31,38.1) rot=(-1,0,0;1.5708rad)
  LinkedObject = -> Screw
  Placement = pos=(191.8,-31,38.1) rot=(-1,0,0;1.5708rad)
  _LinkVersion = 1
FEATURE [App::LinkElement] Link015_i1
  LinkPlacement = pos=(191.8,-31,-38.1) rot=(-1,0,0;1.5708rad)
  LinkedObject = -> Screw
  Placement = pos=(191.8,-31,-38.1) rot=(-1,0,0;1.5708rad)
  _LinkVersion = 1
FEATURE [App::LinkElement] Link015_i2
  LinkPlacement = pos=(191.8,-31,-12.7) rot=(-1,0,0;1.5708rad)
  LinkedObject = -> Screw
  Placement = pos=(191.8,-31,-12.7) rot=(-1,0,0;1.5708rad)
  _LinkVersion = 1
FEATURE [App::LinkElement] Link015_i3
  LinkPlacement = pos=(166.4,-31,-12.7) rot=(-1,0,0;1.5708rad)
  LinkedObject = -> Screw
  Placement = pos=(166.4,-31,-12.7) rot=(-1,0,0;1.5708rad)
  _LinkVersion = 1
FEATURE [App::LinkElement] Link015_i4
  LinkPlacement = pos=(166.4,-31,-38.1) rot=(-1,0,0;1.5708rad)
  LinkedObject = -> Screw
  Placement = pos=(166.4,-31,-38.1) rot=(-1,0,0;1.5708rad)
  _LinkVersion = 1
FEATURE [App::LinkElement] Link015_i5
  LinkPlacement = pos=(166.4,-31,38.1) rot=(-1,0,0;1.5708rad)
  LinkedObject = -> Screw
  Placement = pos=(166.4,-31,38.1) rot=(-1,0,0;1.5708rad)
  _LinkVersion = 1
FEATURE [App::LinkElement] Link015_i6
  LinkPlacement = pos=(191.8,-31,12.7) rot=(-1,0,0;1.5708rad)
  LinkedObject = -> Screw
  Placement = pos=(191.8,-31,12.7) rot=(-1,0,0;1.5708rad)
  _LinkVersion = 1
FEATURE [App::LinkElement] Link015_i7
  LinkPlacement = pos=(166.4,-31,12.7) rot=(-1,0,0;1.5708rad)
  LinkedObject = -> Screw
  Placement = pos=(166.4,-31,12.7) rot=(-1,0,0;1.5708rad)
  _LinkVersion = 1
FEATURE [App::Link] Link015  label="1/4inx1in-Screw 8ct      "
  AutoLinkLabel = true
  AutoPlacement = true
  ElementCount = 8
  ElementList = -> [Link015_i0,Link015_i1,Link015_i2,Link015_i3,Link015_i4,Link015_i5,Link015_i6,Link015_i7]
  LinkPlacement = pos=(-147,31,0) rot=(0,0,1;0rad)
  LinkedObject = -> Screw
  Placement = pos=(-147,31,0) rot=(0,0,1;0rad)
  SyncGroupVisibility = false
  _LinkVersion = 1
FEATURE [Part::FeaturePython] Parts007  # WARN: FeaturePython — macro-defined, semantics opaque (R4)
  Group = -> [Link013,Link015]
  GroupMode = 0
  _LinkVersion = 1
FEATURE [TechDraw::DrawSVGTemplate] Template
  EditableTexts = DrawingTitle1=BK12 & BF12 mounting plates; DrawingTitle2=Count: 2 each; DrawingTitle3=Material: 5mm mild steel; DrawnBy=Andrew <owner>; Revision=V.1.1; Scale=Scale: 1:1; Sheet=Sheet 1 of 1
  Height = 215.9
  Orientation = 1
  Width = 279.4
FEATURE [TechDraw::DrawViewPart] View  label="BF12 left side"
  CoarseView = false
  Direction = (-1,0,0)
  Focus = 100
  HardHidden = false
  IsoCount = 0
  IsoHidden = false
  IsoVisible = false
  LockPosition = false
  Perspective = false
  Rotation = 0
  ScaleType = 0
  SeamHidden = false
  SeamVisible = true
  SmoothHidden = false
  SmoothVisible = true
  Source = -> [Body003]
  X = 66.7193
  XDirection = (0,-1,0)
  Y = 135.524
FEATURE [TechDraw::DrawViewPart] View001  label="BK12 left & right side"
  CoarseView = false
  Direction = (-1,0,0)
  Focus = 100
  HardHidden = false
  IsoCount = 0
  IsoHidden = false
  IsoVisible = false
  LockPosition = false
  Perspective = false
  Rotation = 0
  ScaleType = 0
  SeamHidden = false
  SeamVisible = true
  SmoothHidden = false
  SmoothVisible = true
  Source = -> [Body005]
  X = 195.919
  XDirection = (0,-1,0)
  Y = 134.656
FEATURE [TechDraw::DrawViewPart] View002  label="BF12 & BK12 overview"
  CoarseView = false
  Direction = (-0.577,-0.577,0.577)
  Focus = 100
  HardHidden = false
  IsoCount = 0
  IsoHidden = false
  IsoVisible = false
  LockPosition = false
  Perspective = false
  Rotation = 0
  Scale = 0.7
  ScaleType = 0
  SeamHidden = false
  SeamVisible = true
  SmoothHidden = false
  SmoothVisible = true
  Source = -> [Body003,Body005]
  X = 63.6398
  XDirection = (0.707,-0.707,0)
  Y = 55.6586
FEATURE [Sketcher::SketchObject] Sketch004
  ExternalGeometry = -> [Fillet]
  FullyConstrained = false
  MapMode = 5
  Placement = pos=(0,0,0) rot=(-1,0,0;1.5708rad)
  Support = -> [Fillet]
  sketch-geometry (4):
    g0: Circle CenterX=-14.5 CenterY=-32.1 CenterZ=0 NormalX=0 NormalY=0 NormalZ=1 AngleXU=0 Radius=1.25
    g1: Circle CenterX=-14.5 CenterY=-44.1 CenterZ=0 NormalX=0 NormalY=0 NormalZ=1 AngleXU=0 Radius=1.25
    g2: LineSegment [constr] StartX=60.7569 StartY=-38.1 StartZ=0 EndX=-84.1022 EndY=-38.1 EndZ=0
    g3: Circle CenterX=0.25 CenterY=-38.1 CenterZ=0 NormalX=0 NormalY=0 NormalZ=1 AngleXU=0 Radius=2.75
  constraints (10):
    c: Equal(g0,g1)
    c: Symmetric(g0,g1,g2)
    c: Diameter(g0) = 2.5
    c: DistanceX(g-4,g1) = 43
    c: DistanceY(g1,g0) = 12
    c: PointOnObject(g3,g2)
    c: Diameter(g3) = 5.5
    c: Vertical(g-5,g3)
    c: PointOnObject(g-3,g2)
    c: Horizontal(g2)
FEATURE [PartDesign::Pocket] Pocket
  BaseFeature = -> Fillet
  ClaimChildren = false
  Fit = 0
  FitJoin = 0
  InnerFit = 0
  InnerFitJoin = 0
  InnerTaperAngle = 0
  InnerTaperAngleRev = 0
  Length = 5
  Length2 = 100
  Linearize = true
  NewSolid = false
  Placement = pos=(0,0,0) rot=(1,0,0;1.5708rad)
  Profile = -> Sketch004
  Refine = true
  Suppress = false
  Type = 1
  _ProfileBasedVersion = 1
FEATURE [PartDesign::Body] Body006  label="motor plate"
  AutoGroupSolids = false
  ExportMode = 0
  Group = -> [Sketch002,Pad002,Fillet,Sketch004,Pocket]
  Origin = -> Origin006
  Tip = -> Pocket
  _ExportChildren = -> [Pad002,Fillet,Pocket]
  _GroupVersion = 1
FEATURE [App::DocumentObjectGroup] Group  label="Components"
  ExportMode = 1
  Group = -> [Body,Body001,Body002,Body003,Body004,Body005,Body006,Screw,Screw001,Body007]
  _GroupVersion = 1
FEATURE [TechDraw::DrawSVGTemplate] Template001
  EditableTexts = DrawingTitle1=Y axis motor holding plate; DrawingTitle2=Count: 2; DrawingTitle3=Material: 1/4" aluminum; DrawnBy=Andrew <owner>; Revision=V.1.0; Scale=Scale 1:1; Sheet=Sheet 1 of 1
  Height = 215.9
  Orientation = 1
  Width = 279.4
FEATURE [TechDraw::DrawViewPart] View003  label="Motor plate front"
  CoarseView = false
  Direction = (0,-1,0)
  Focus = 100
  HardHidden = false
  IsoCount = 0
  IsoHidden = false
  IsoVisible = false
  LockPosition = false
  Perspective = false
  Rotation = 0
  ScaleType = 0
  SeamHidden = false
  SeamVisible = true
  SmoothHidden = false
  SmoothVisible = true
  Source = -> [Body006]
  X = 129.635
  XDirection = (1,0,0)
  Y = 130.094
FEATURE [TechDraw::DrawViewDimension] Dimension018
  Arbitrary = false
  ArbitraryTolerances = false
  EqualTolerance = true
  FormatSpec = ⌀%.2f
  FormatSpecOverTolerance = %+.2f
  FormatSpecUnderTolerance = %+.2f
  Inverted = false
  LockPosition = false
  MeasureType = 1
  OverTolerance = 0
  References2D = -> [View003]
  Rotation = 0
  ScaleType = 0
  TheoreticalExact = false
  Type = 5
  UnderTolerance = 0
  X = 0
  Y = 0
FEATURE [TechDraw::DrawViewDimension] Dimension019
  Arbitrary = false
  ArbitraryTolerances = false
  EqualTolerance = true
  FormatSpec = ⌀%.2f
  FormatSpecOverTolerance = %+.2f
  FormatSpecUnderTolerance = %+.2f
  Inverted = false
  LockPosition = false
  MeasureType = 1
  OverTolerance = 0
  References2D = -> [View003]
  Rotation = 0
  ScaleType = 0
  TheoreticalExact = false
  Type = 5
  UnderTolerance = 0
  X = 6.54242
  Y = 48.8165
FEATURE [TechDraw::DrawViewDimension] Dimension020
  Arbitrary = true
  ArbitraryTolerances = false
  EqualTolerance = true
  FormatSpec = 4x M5
  FormatSpecOverTolerance = %+.2f
  FormatSpecUnderTolerance = %+.2f
  Inverted = false
  LockPosition = false
  MeasureType = 1
  OverTolerance = 0
  References2D = -> [View003]
  Rotation = 0
  ScaleType = 0
  TheoreticalExact = false
  Type = 5
  UnderTolerance = 0
  X = -37.9964
  Y = 21.3887
FEATURE [TechDraw::DrawViewDimension] Dimension021
  Arbitrary = true
  ArbitraryTolerances = false
  EqualTolerance = true
  FormatSpec = 2x M3
  FormatSpecOverTolerance = %+.2f
  FormatSpecUnderTolerance = %+.2f
  Inverted = false
  LockPosition = false
  MeasureType = 1
  OverTolerance = 0
  References2D = -> [View003]
  Rotation = 0
  ScaleType = 0
  TheoreticalExact = false
  Type = 5
  UnderTolerance = 0
  X = -3.52284
  Y = 57.372
FEATURE [TechDraw::DrawViewDimension] Dimension022
  Arbitrary = false
  ArbitraryTolerances = false
  EqualTolerance = true
  FormatSpec = 8x ⌀%.2f
  FormatSpecOverTolerance = %+.2f
  FormatSpecUnderTolerance = %+.2f
  Inverted = false
  LockPosition = false
  MeasureType = 1
  OverTolerance = 0
  References2D = -> [View003]
  Rotation = 0
  ScaleType = 0
  TheoreticalExact = false
  Type = 5
  UnderTolerance = 0
  X = 29.9442
  Y = 0.503263
FEATURE [TechDraw::DrawViewDimension] Dimension023
  Arbitrary = false
  ArbitraryTolerances = false
  EqualTolerance = true
  FormatSpec = %.2f
  FormatSpecOverTolerance = %+.2f
  FormatSpecUnderTolerance = %+.2f
  Inverted = false
  LockPosition = false
  MeasureType = 1
  OverTolerance = 0
  References2D = -> [View003]
  Rotation = 0
  ScaleType = 0
  TheoreticalExact = false
  Type = 1
  UnderTolerance = 0
  X = -0.503263
  Y = 69.1822
FEATURE [TechDraw::DrawViewDimension] Dimension024
  Arbitrary = false
  ArbitraryTolerances = false
  EqualTolerance = true
  FormatSpec = %.2f
  FormatSpecOverTolerance = %+.2f
  FormatSpecUnderTolerance = %+.2f
  Inverted = false
  LockPosition = false
  MeasureType = 1
  OverTolerance = 0
  References2D = -> [View003]
  Rotation = 0
  ScaleType = 0
  TheoreticalExact = false
  Type = 2
  UnderTolerance = 0
  X = -84.9409
  Y = -2.26469
FEATURE [TechDraw::DrawViewDimension] Dimension025
  Arbitrary = false
  ArbitraryTolerances = false
  EqualTolerance = true
  FormatSpec = 4x R%.2f
  FormatSpecOverTolerance = %+.2f
  FormatSpecUnderTolerance = %+.2f
  Inverted = false
  LockPosition = false
  MeasureType = 1
  OverTolerance = 0
  References2D = -> [View003]
  Rotation = 0
  ScaleType = 0
  TheoreticalExact = false
  Type = 4
  UnderTolerance = 0
  X = 69.1987
  Y = 61.9014
FEATURE [TechDraw::DrawViewDimension] Dimension026
  Arbitrary = false
  ArbitraryTolerances = false
  EqualTolerance = true
  FormatSpec = %.2f
  FormatSpecOverTolerance = %+.2f
  FormatSpecUnderTolerance = %+.2f
  Inverted = false
  LockPosition = false
  MeasureType = 1
  OverTolerance = 0
  References2D = -> [View003]
  Rotation = 0
  ScaleType = 0
  TheoreticalExact = false
  Type = 1
  UnderTolerance = 0
  X = -23.3
  Y = -38.65
FEATURE [TechDraw::DrawViewDimension] Dimension027
  Arbitrary = false
  ArbitraryTolerances = false
  EqualTolerance = true
  FormatSpec = %.2f
  FormatSpecOverTolerance = %+.2f
  FormatSpecUnderTolerance = %+.2f
  Inverted = false
  LockPosition = false
  MeasureType = 1
  OverTolerance = 0
  References2D = -> [View003]
  Rotation = 0
  ScaleType = 0
  TheoreticalExact = false
  Type = 2
  UnderTolerance = 0
  X = -74.8344
  Y = -13.492
FEATURE [TechDraw::DrawViewDimension] Dimension028
  Arbitrary = false
  ArbitraryTolerances = false
  EqualTolerance = true
  FormatSpec = %.2f
  FormatSpecOverTolerance = %+.2f
  FormatSpecUnderTolerance = %+.2f
  Inverted = false
  LockPosition = false
  MeasureType = 1
  OverTolerance = 0
  References2D = -> [View003]
  Rotation = 0
  ScaleType = 0
  TheoreticalExact = false
  Type = 1
  UnderTolerance = 0
  X = -34.5608
  Y = -52.7837
FEATURE [TechDraw::DrawViewDimension] Dimension029
  Arbitrary = false
  ArbitraryTolerances = false
  EqualTolerance = true
  FormatSpec = %.2f
  FormatSpecOverTolerance = %+.2f
  FormatSpecUnderTolerance = %+.2f
  Inverted = false
  LockPosition = false
  MeasureType = 1
  OverTolerance = 0
  References2D = -> [View003]
  Rotation = 0
  ScaleType = 0
  TheoreticalExact = false
  Type = 2
  UnderTolerance = 0
  X = -74.7768
  Y = -42.7479
FEATURE [TechDraw::DrawViewDimension] Dimension030
  Arbitrary = false
  ArbitraryTolerances = false
  EqualTolerance = true
  FormatSpec = %.2f
  FormatSpecOverTolerance = %+.2f
  FormatSpecUnderTolerance = %+.2f
  Inverted = false
  LockPosition = false
  MeasureType = 1
  OverTolerance = 0
  References2D = -> [View003]
  Rotation = 0
  ScaleType = 0
  TheoreticalExact = false
  Type = 1
  UnderTolerance = 0
  X = -31.6712
  Y = -4.38512
FEATURE [TechDraw::DrawViewDimension] Dimension031
  Arbitrary = false
  ArbitraryTolerances = false
  EqualTolerance = true
  FormatSpec = %.2f
  FormatSpecOverTolerance = %+.2f
  FormatSpecUnderTolerance = %+.2f
  Inverted = false
  LockPosition = false
  MeasureType = 1
  OverTolerance = 0
  References2D = -> [View003]
  Rotation = 0
  ScaleType = 0
  TheoreticalExact = false
  Type = 2
  UnderTolerance = 0
  X = -63.2896
  Y = -25.5994
FEATURE [TechDraw::DrawViewDimension] Dimension032
  Arbitrary = false
  ArbitraryTolerances = false
  EqualTolerance = true
  FormatSpec = %.2f
  FormatSpecOverTolerance = %+.2f
  FormatSpecUnderTolerance = %+.2f
  Inverted = false
  LockPosition = false
  MeasureType = 1
  OverTolerance = 0
  References2D = -> [View003]
  Rotation = 0
  ScaleType = 0
  TheoreticalExact = false
  Type = 1
  UnderTolerance = 0
  X = 32.5594
  Y = -26.1552
FEATURE [TechDraw::DrawViewDimension] Dimension033
  Arbitrary = false
  ArbitraryTolerances = false
  EqualTolerance = true
  FormatSpec = %.2f
  FormatSpecOverTolerance = %+.2f
  FormatSpecUnderTolerance = %+.2f
  Inverted = false
  LockPosition = false
  MeasureType = 1
  OverTolerance = 0
  References2D = -> [View003]
  Rotation = 0
  ScaleType = 0
  TheoreticalExact = false
  Type = 2
  UnderTolerance = 0
  X = 50.0833
  Y = -21.495
FEATURE [TechDraw::DrawViewDimension] Dimension034
  Arbitrary = false
  ArbitraryTolerances = false
  EqualTolerance = true
  FormatSpec = %.2f
  FormatSpecOverTolerance = %+.2f
  FormatSpecUnderTolerance = %+.2f
  Inverted = false
  LockPosition = false
  MeasureType = 1
  OverTolerance = 0
  References2D = -> [View003]
  Rotation = 0
  ScaleType = 0
  TheoreticalExact = false
  Type = 2
  UnderTolerance = 0
  X = 49.8536
  Y = 2.29707
FEATURE [TechDraw::DrawViewDimension] Dimension035
  Arbitrary = false
  ArbitraryTolerances = false
  EqualTolerance = true
  FormatSpec = %.2f
  FormatSpecOverTolerance = %+.2f
  FormatSpecUnderTolerance = %+.2f
  Inverted = false
  LockPosition = false
  MeasureType = 1
  OverTolerance = 0
  References2D = -> [View003]
  Rotation = 0
  ScaleType = 0
  TheoreticalExact = false
  Type = 2
  UnderTolerance = 0
  X = 49.8536
  Y = 27.2377
FEATURE [TechDraw::DrawViewDimension] Dimension036
  Arbitrary = false
  ArbitraryTolerances = false
  EqualTolerance = true
  FormatSpec = %.2f
  FormatSpecOverTolerance = %+.2f
  FormatSpecUnderTolerance = %+.2f
  Inverted = false
  LockPosition = false
  MeasureType = 1
  OverTolerance = 0
  References2D = -> [View003]
  Rotation = 0
  ScaleType = 0
  TheoreticalExact = false
  Type = 2
  UnderTolerance = 0
  X = 50.15
  Y = -41.9232
FEATURE [TechDraw::DrawViewDimension] Dimension037
  Arbitrary = false
  ArbitraryTolerances = false
  EqualTolerance = true
  FormatSpec = %.2f
  FormatSpecOverTolerance = %+.2f
  FormatSpecUnderTolerance = %+.2f
  Inverted = false
  LockPosition = false
  MeasureType = 1
  OverTolerance = 0
  References2D = -> [View003]
  Rotation = 0
  ScaleType = 0
  TheoreticalExact = false
  Type = 2
  UnderTolerance = 0
  X = -26.6745
  Y = 39.4782
FEATURE [TechDraw::DrawViewDimension] Dimension038
  Arbitrary = false
  ArbitraryTolerances = false
  EqualTolerance = true
  FormatSpec = %.2f
  FormatSpecOverTolerance = %+.2f
  FormatSpecUnderTolerance = %+.2f
  Inverted = false
  LockPosition = false
  MeasureType = 1
  OverTolerance = 0
  References2D = -> [View003]
  Rotation = 0
  ScaleType = 0
  TheoreticalExact = false
  Type = 1
  UnderTolerance = 0
  X = -6.66559
  Y = 27.9791
FEATURE [TechDraw::DrawViewDimension] Dimension039
  Arbitrary = false
  ArbitraryTolerances = false
  EqualTolerance = true
  FormatSpec = %.2f
  FormatSpecOverTolerance = %+.2f
  FormatSpecUnderTolerance = %+.2f
  Inverted = false
  LockPosition = false
  MeasureType = 1
  OverTolerance = 0
  References2D = -> [View003]
  Rotation = 0
  ScaleType = 0
  TheoreticalExact = false
  Type = 1
  UnderTolerance = 0
  X = 9.825
  Y = 27.7831
FEATURE [TechDraw::DrawPage] Page001  label="Motor plate"
  KeepUpdated = true
  NextBalloonIndex = 1
  ProjectionType = 0
  Template = -> Template001
  Views = -> [View003,Dimension018,Dimension019,Dimension020,Dimension021,Dimension022,Dimension023,Dimension024,Dimension025,Dimension026,Dimension027,Dimension028,Dimension029,Dimension030,Dimension031,Dimension032,Dimension033,Dimension034,Dimension035,Dimension036,Dimension037,Dimension038,Dimension039]
FEATURE [TechDraw::DrawSVGTemplate] Template002
  EditableTexts = DrawingTitle1=Base Front Plate; DrawingTitle2=Count: 2; DrawingTitle3=Material: 1/4" Acrilic or Aluminum; DrawnBy=Andrew <owner>; Revision=V.1.0; Scale=Scale 1:1; Sheet=Sheet 1 of 1
  Height = 215.9
  Orientation = 1
  Width = 279.4
FEATURE [TechDraw::DrawViewPart] View004  label="Front plate front"
  CoarseView = false
  Direction = (0,-1,0)
  Focus = 100
  HardHidden = false
  IsoCount = 0
  IsoHidden = false
  IsoVisible = false
  LockPosition = false
  Perspective = false
  Rotation = 0
  ScaleType = 0
  SeamHidden = false
  SeamVisible = true
  SmoothHidden = false
  SmoothVisible = true
  Source = -> [Body007]
  X = 118.311
  XDirection = (1,0,0)
  Y = 134.875
FEATURE [TechDraw::DrawViewDimension] Dimension040
  Arbitrary = false
  ArbitraryTolerances = false
  EqualTolerance = true
  FormatSpec = %.2f
  FormatSpecOverTolerance = %+.2f
  FormatSpecUnderTolerance = %+.2f
  Inverted = false
  LockPosition = false
  MeasureType = 1
  OverTolerance = 0
  References2D = -> [View004]
  Rotation = 0
  ScaleType = 0
  TheoreticalExact = false
  Type = 2
  UnderTolerance = 0
  X = 8.83147
  Y = -24.1418
FEATURE [TechDraw::DrawViewDimension] Dimension041
  Arbitrary = false
  ArbitraryTolerances = false
  EqualTolerance = true
  FormatSpec = %.2f
  FormatSpecOverTolerance = %+.2f
  FormatSpecUnderTolerance = %+.2f
  Inverted = false
  LockPosition = false
  MeasureType = 1
  OverTolerance = 0
  References2D = -> [View004]
  Rotation = 0
  ScaleType = 0
  TheoreticalExact = false
  Type = 1
  UnderTolerance = 0
  X = 31.8484
  Y = -57.224
FEATURE [TechDraw::DrawViewDimension] Dimension042
  Arbitrary = false
  ArbitraryTolerances = false
  EqualTolerance = true
  FormatSpec = %.2f
  FormatSpecOverTolerance = %+.2f
  FormatSpecUnderTolerance = %+.2f
  Inverted = false
  LockPosition = false
  MeasureType = 1
  OverTolerance = 0
  References2D = -> [View004]
  Rotation = 0
  ScaleType = 0
  TheoreticalExact = false
  Type = 2
  UnderTolerance = 0
  X = 65.2479
  Y = -42.437
FEATURE [TechDraw::DrawViewDimension] Dimension043
  Arbitrary = false
  ArbitraryTolerances = false
  EqualTolerance = true
  FormatSpec = %.2f
  FormatSpecOverTolerance = %+.2f
  FormatSpecUnderTolerance = %+.2f
  Inverted = false
  LockPosition = false
  MeasureType = 1
  OverTolerance = 0
  References2D = -> [View004]
  Rotation = 0
  ScaleType = 0
  TheoreticalExact = false
  Type = 1
  UnderTolerance = 0
  X = 50.6468
  Y = -57.2897
FEATURE [TechDraw::DrawViewDimension] Dimension044
  Arbitrary = false
  ArbitraryTolerances = false
  EqualTolerance = true
  FormatSpec = %.2f
  FormatSpecOverTolerance = %+.2f
  FormatSpecUnderTolerance = %+.2f
  Inverted = false
  LockPosition = false
  MeasureType = 1
  OverTolerance = 0
  References2D = -> [View004]
  Rotation = 0
  ScaleType = 0
  TheoreticalExact = false
  Type = 1
  UnderTolerance = 0
  X = 0.524233
  Y = 63.3038
FEATURE [TechDraw::DrawViewDimension] Dimension045
  Arbitrary = false
  ArbitraryTolerances = false
  EqualTolerance = true
  FormatSpec = %.2f
  FormatSpecOverTolerance = %+.2f
  FormatSpecUnderTolerance = %+.2f
  Inverted = false
  LockPosition = false
  MeasureType = 1
  OverTolerance = 0
  References2D = -> [View004]
  Rotation = 0
  ScaleType = 0
  TheoreticalExact = false
  Type = 2
  UnderTolerance = 0
  X = -69.4795
  Y = 0
FEATURE [TechDraw::DrawViewDimension] Dimension046
  Arbitrary = false
  ArbitraryTolerances = false
  EqualTolerance = true
  FormatSpec = %.2f
  FormatSpecOverTolerance = %+.2f
  FormatSpecUnderTolerance = %+.2f
  Inverted = false
  LockPosition = false
  MeasureType = 1
  OverTolerance = 0
  References2D = -> [View004]
  Rotation = 0
  ScaleType = 0
  TheoreticalExact = false
  Type = 2
  UnderTolerance = 0
  X = 8.91535
  Y = 8.73721
FEATURE [TechDraw::DrawViewDimension] Dimension047
  Arbitrary = false
  ArbitraryTolerances = false
  EqualTolerance = true
  FormatSpec = 4x R%.2f
  FormatSpecOverTolerance = %+.2f
  FormatSpecUnderTolerance = %+.2f
  Inverted = false
  LockPosition = false
  MeasureType = 1
  OverTolerance = 0
  References2D = -> [View004]
  Rotation = 0
  ScaleType = 0
  TheoreticalExact = false
  Type = 4
  UnderTolerance = 0
  X = 66.892
  Y = 61.2443
FEATURE [TechDraw::DrawViewDimension] Dimension048
  Arbitrary = false
  ArbitraryTolerances = false
  EqualTolerance = true
  FormatSpec = 8x ⌀%.2f
  FormatSpecOverTolerance = %+.2f
  FormatSpecUnderTolerance = %+.2f
  Inverted = false
  LockPosition = false
  MeasureType = 1
  OverTolerance = 0
  References2D = -> [View004]
  Rotation = 0
  ScaleType = 0
  TheoreticalExact = false
  Type = 5
  UnderTolerance = 0
  X = 27.7843
  Y = 26.5611
FEATURE [TechDraw::DrawPage] Page002  label="Front plate"
  KeepUpdated = true
  NextBalloonIndex = 1
  ProjectionType = 0
  Template = -> Template002
  Views = -> [View004,Dimension040,Dimension041,Dimension042,Dimension043,Dimension044,Dimension045,Dimension046,Dimension047,Dimension048]
FEATURE [TechDraw::DrawViewAnnotation] Annotation
  Font = osifont
  LineSpace = 80
  LockPosition = false
  MaxWidth = -1
  Rotation = 0
  ScaleType = 0
  Text = BF12 Left and Right sides  | are just mirrored copies  | of the same part
  TextSize = 5
  TextStyle = 0
  X = 127.571
  Y = 80.6608
FEATURE [TechDraw::DrawViewDimension] Dimension050
  Arbitrary = false
  ArbitraryTolerances = false
  EqualTolerance = true
  FormatSpec = %.2f
  FormatSpecOverTolerance = %+.2f
  FormatSpecUnderTolerance = %+.2f
  Inverted = false
  LockPosition = false
  MeasureType = 1
  OverTolerance = 0
  References2D = -> [View001]
  Rotation = 0
  ScaleType = 0
  TheoreticalExact = false
  Type = 2
  UnderTolerance = 0
  X = 30.5711
  Y = -26.1686
FEATURE [TechDraw::DrawViewDimension] Dimension051
  Arbitrary = false
  ArbitraryTolerances = false
  EqualTolerance = true
  FormatSpec = %.2f
  FormatSpecOverTolerance = %+.2f
  FormatSpecUnderTolerance = %+.2f
  Inverted = false
  LockPosition = false
  MeasureType = 1
  OverTolerance = 0
  References2D = -> [View001]
  Rotation = 0
  ScaleType = 0
  TheoreticalExact = false
  Type = 2
  UnderTolerance = 0
  X = -32.5335
  Y = 0.139959
FEATURE [TechDraw::DrawViewDimension] Dimension052
  Arbitrary = false
  ArbitraryTolerances = false
  EqualTolerance = true
  FormatSpec = %.2f
  FormatSpecOverTolerance = %+.2f
  FormatSpecUnderTolerance = %+.2f
  Inverted = false
  LockPosition = false
  MeasureType = 1
  OverTolerance = 0
  References2D = -> [View001]
  Rotation = 0
  ScaleType = 0
  TheoreticalExact = false
  Type = 2
  UnderTolerance = 0
  X = -41.3624
  Y = 2.80182
FEATURE [TechDraw::DrawViewDimension] Dimension053
  Arbitrary = false
  ArbitraryTolerances = false
  EqualTolerance = true
  FormatSpec = %.2f
  FormatSpecOverTolerance = %+.2f
  FormatSpecUnderTolerance = %+.2f
  Inverted = false
  LockPosition = false
  MeasureType = 1
  OverTolerance = 0
  References2D = -> [View001]
  Rotation = 0
  ScaleType = 0
  TheoreticalExact = false
  Type = 2
  UnderTolerance = 0
  X = 36.6058
  Y = -0.34562
FEATURE [TechDraw::DrawViewDimension] Dimension054
  Arbitrary = false
  ArbitraryTolerances = false
  EqualTolerance = true
  FormatSpec = %.2f
  FormatSpecOverTolerance = %+.2f
  FormatSpecUnderTolerance = %+.2f
  Inverted = false
  LockPosition = false
  MeasureType = 1
  OverTolerance = 0
  References2D = -> [View001]
  Rotation = 0
  ScaleType = 0
  TheoreticalExact = false
  Type = 1
  UnderTolerance = 0
  X = -1.37824
  Y = 39.9469
FEATURE [TechDraw::DrawViewDimension] Dimension055
  Arbitrary = false
  ArbitraryTolerances = false
  EqualTolerance = true
  FormatSpec = %.2f
  FormatSpecOverTolerance = %+.2f
  FormatSpecUnderTolerance = %+.2f
  Inverted = false
  LockPosition = false
  MeasureType = 1
  OverTolerance = 0
  References2D = -> [View001]
  Rotation = 0
  ScaleType = 0
  TheoreticalExact = false
  Type = 1
  UnderTolerance = 0
  X = -1.4562
  Y = 45.652
FEATURE [TechDraw::DrawViewDimension] Dimension056
  Arbitrary = false
  ArbitraryTolerances = false
  EqualTolerance = true
  FormatSpec = %.2f
  FormatSpecOverTolerance = %+.2f
  FormatSpecUnderTolerance = %+.2f
  Inverted = false
  LockPosition = false
  MeasureType = 1
  OverTolerance = 0
  References2D = -> [View001]
  Rotation = 0
  ScaleType = 0
  TheoreticalExact = false
  Type = 1
  UnderTolerance = 0
  X = 0.606751
  Y = 52.4925
FEATURE [TechDraw::DrawViewDimension] Dimension057
  Arbitrary = true
  ArbitraryTolerances = false
  EqualTolerance = true
  FormatSpec = 4x 1/4-20
  FormatSpecOverTolerance = %+.2f
  FormatSpecUnderTolerance = %+.2f
  Inverted = false
  LockPosition = false
  MeasureType = 1
  OverTolerance = 0
  References2D = -> [View001]
  Rotation = 0
  ScaleType = 0
  TheoreticalExact = false
  Type = 4
  UnderTolerance = 0
  X = 10.7503
  Y = -7.99381
FEATURE [TechDraw::DrawViewDimension] Dimension
  Arbitrary = false
  ArbitraryTolerances = false
  EqualTolerance = true
  FormatSpec = 4x ⌀%.1f ˅⌀9.5
  FormatSpecOverTolerance = %+.2f
  FormatSpecUnderTolerance = %+.2f
  Inverted = false
  LockPosition = false
  MeasureType = 1
  OverTolerance = 0
  References2D = -> [View001]
  Rotation = 0
  ScaleType = 0
  TheoreticalExact = false
  Type = 5
  UnderTolerance = 0
  X = -5.35984
  Y = -3.25419
FEATURE [TechDraw::DrawViewDimension] Dimension058
  Arbitrary = false
  ArbitraryTolerances = false
  EqualTolerance = true
  FormatSpec = 2x ⌀%.1f ˅⌀9.5
  FormatSpecOverTolerance = %+.2f
  FormatSpecUnderTolerance = %+.2f
  Inverted = false
  LockPosition = false
  MeasureType = 1
  OverTolerance = 0
  References2D = -> [View]
  Rotation = 0
  ScaleType = 0
  TheoreticalExact = false
  Type = 5
  UnderTolerance = 0
  X = -3.63703
  Y = -2.67992
FEATURE [TechDraw::DrawViewDimension] Dimension059
  Arbitrary = true
  ArbitraryTolerances = false
  EqualTolerance = true
  FormatSpec = 4x 1/4-20
  FormatSpecOverTolerance = %+.2f
  FormatSpecUnderTolerance = %+.2f
  Inverted = false
  LockPosition = false
  MeasureType = 1
  OverTolerance = 0
  References2D = -> [View]
  Rotation = 0
  ScaleType = 0
  TheoreticalExact = false
  Type = 4
  UnderTolerance = 0
  X = 8.99687
  Y = -7.84833
FEATURE [TechDraw::DrawViewDimension] Dimension060
  Arbitrary = false
  ArbitraryTolerances = false
  EqualTolerance = true
  FormatSpec = %.2f
  FormatSpecOverTolerance = %+.2f
  FormatSpecUnderTolerance = %+.2f
  Inverted = false
  LockPosition = false
  MeasureType = 1
  OverTolerance = 0
  References2D = -> [View]
  Rotation = 0
  ScaleType = 0
  TheoreticalExact = false
  Type = 2
  UnderTolerance = 0
  X = 21.7993
  Y = -26.2377
FEATURE [TechDraw::DrawViewDimension] Dimension061
  Arbitrary = false
  ArbitraryTolerances = false
  EqualTolerance = true
  FormatSpec = %.2f
  FormatSpecOverTolerance = %+.2f
  FormatSpecUnderTolerance = %+.2f
  Inverted = false
  LockPosition = false
  MeasureType = 1
  OverTolerance = 0
  References2D = -> [View]
  Rotation = 0
  ScaleType = 0
  TheoreticalExact = false
  Type = 2
  UnderTolerance = 0
  X = 30.686
  Y = -0.997595
FEATURE [TechDraw::DrawViewDimension] Dimension062
  Arbitrary = false
  ArbitraryTolerances = false
  EqualTolerance = true
  FormatSpec = %.2f
  FormatSpecOverTolerance = %+.2f
  FormatSpecUnderTolerance = %+.2f
  Inverted = false
  LockPosition = false
  MeasureType = 1
  OverTolerance = 0
  References2D = -> [View]
  Rotation = 0
  ScaleType = 0
  TheoreticalExact = false
  Type = 2
  UnderTolerance = 0
  X = -23.8048
  Y = 0.675767
FEATURE [TechDraw::DrawViewDimension] Dimension063
  Arbitrary = false
  ArbitraryTolerances = false
  EqualTolerance = true
  FormatSpec = %.2f
  FormatSpecOverTolerance = %+.2f
  FormatSpecUnderTolerance = %+.2f
  Inverted = false
  LockPosition = false
  MeasureType = 1
  OverTolerance = 0
  References2D = -> [View]
  Rotation = 0
  ScaleType = 0
  TheoreticalExact = false
  Type = 1
  UnderTolerance = 0
  X = -11.8521
  Y = 39.7283
FEATURE [TechDraw::DrawViewDimension] Dimension064
  Arbitrary = false
  ArbitraryTolerances = false
  EqualTolerance = true
  FormatSpec = %.2f
  FormatSpecOverTolerance = %+.2f
  FormatSpecUnderTolerance = %+.2f
  Inverted = false
  LockPosition = false
  MeasureType = 1
  OverTolerance = 0
  References2D = -> [View]
  Rotation = 0
  ScaleType = 0
  TheoreticalExact = false
  Type = 1
  UnderTolerance = 0
  X = -2.7281
  Y = 18.1325
FEATURE [TechDraw::DrawViewDimension] Dimension065
  Arbitrary = false
  ArbitraryTolerances = false
  EqualTolerance = true
  FormatSpec = %.2f
  FormatSpecOverTolerance = %+.2f
  FormatSpecUnderTolerance = %+.2f
  Inverted = false
  LockPosition = false
  MeasureType = 1
  OverTolerance = 0
  References2D = -> [View]
  Rotation = 0
  ScaleType = 0
  TheoreticalExact = false
  Type = 1
  UnderTolerance = 0
  X = -1.59519
  Y = 46.5495
FEATURE [TechDraw::DrawPage] Page  label="BK12 & BF12 plates"
  KeepUpdated = true
  NextBalloonIndex = 1
  ProjectionType = 0
  Template = -> Template
  Views = -> [View,View001,View002,Annotation,Dimension050,Dimension051,Dimension052,Dimension053,Dimension054,Dimension055,Dimension056,Dimension057,Dimension,Dimension058,Dimension059,Dimension060,Dimension061,Dimension062,Dimension063,Dimension064,Dimension065]
FEATURE [App::DocumentObjectGroup] Group002  label="Drawings"
  ExportMode = 1
  Group = -> [Page,Page001,Page002]
  _GroupVersion = 1
FEATURE [App::DocumentObjectGroup] Group001  label="Assemblies"
  ExportMode = 1
  Group = -> [Assembly,Assembly001,Assembly002,Assembly003,Assembly004,Assembly005,Assembly006,Assembly007]
  _GroupVersion = 1
FEATURE [Part::FeaturePython] Assembly  label="BK12R Assembly"  # WARN: FeaturePython — macro-defined, semantics opaque (R4)
  AutoRelax = true
  BuildShape = 0
  Freeze = false
  Group = -> [Constraints,Elements,Parts]
  Verbose = false
  _LinkVersion = 1
  _SolverType = 1
  _Version = 1
FEATURE [App::FeaturePython] Constraints  # WARN: FeaturePython — macro-defined, semantics opaque (R4)
  Group = -> [Constraint,Constraint031,Constraint032,Constraint033,Constraint034]
  _LinkVersion = 1
  _Version = 1
FEATURE [App::FeaturePython] Elements  # WARN: FeaturePython — macro-defined, semantics opaque (R4)
  Group = -> [Element,_Element048,_Element049,_Element050,_Element051,_Element052,_Element053,_Element054,_Element055]
  _LinkVersion = 1
FEATURE [Part::FeaturePython] Element  label="BK-tr-mate"  # link proxy (typed FeaturePython)
  Detach = false
  LinkTransform = true
  LinkedObject = -> Link [Hole002.Edge42]
  _LinkVersion = 1
  _Parent = -> Elements
FEATURE [App::FeaturePython] Constraint  label="Locked"  # WARN: FeaturePython — macro-defined, semantics opaque (R4)
  Disabled = false
  Group = -> [ElementLink]
  _ConstraintType = 0
  _LinkVersion = 1
  _Parent = -> Constraints
FEATURE [App::FeaturePython] ElementLink  label="BK-tr-mate"  # link proxy (typed FeaturePython)
  LinkTransform = true
  LinkedObject = -> Element
  _LinkVersion = 1
  _Parent = -> Constraint
FEATURE [Part::FeaturePython] Assembly001  label="BK12L Assembly"  # WARN: FeaturePython — macro-defined, semantics opaque (R4)
  AutoRelax = true
  BuildShape = 0
  Freeze = false
  Group = -> [Constraints001,Elements001,Parts001]
  Placement = pos=(-17,2.02656e-06,0) rot=(0,0,1;0rad)
  Verbose = false
  _LinkVersion = 1
  _SolverType = 1
  _Version = 1
FEATURE [App::FeaturePython] Constraints001  # WARN: FeaturePython — macro-defined, semantics opaque (R4)
  Group = -> [Constraint001,Constraint025,Constraint026,Constraint027,Constraint028]
  _LinkVersion = 1
  _Version = 1
FEATURE [App::FeaturePython] Elements001  # WARN: FeaturePython — macro-defined, semantics opaque (R4)
  Group = -> [Element001,_Element036,_Element037,_Element038,_Element039,_Element040,_Element041,_Element042,_Element043]
  _LinkVersion = 1
FEATURE [Part::FeaturePython] Element001  label="BK-tr-mate"  # link proxy (typed FeaturePython)
  Detach = false
  LinkTransform = true
  LinkedObject = -> Link001 [Hole003.Edge25]
  _LinkVersion = 1
  _Parent = -> Elements001
FEATURE [App::FeaturePython] Constraint001  label="Locked001"  # WARN: FeaturePython — macro-defined, semantics opaque (R4)
  Disabled = false
  Group = -> [ElementLink001]
  _ConstraintType = 0
  _LinkVersion = 1
  _Parent = -> Constraints001
FEATURE [App::FeaturePython] ElementLink001  label="BK-tr-mate"  # link proxy (typed FeaturePython)
  LinkTransform = true
  LinkedObject = -> Element001
  _LinkVersion = 1
  _Parent = -> Constraint001
FEATURE [Part::FeaturePython] Assembly002  label="BF12L Assembly"  # WARN: FeaturePython — macro-defined, semantics opaque (R4)
  AutoRelax = true
  BuildShape = 0
  Freeze = false
  Group = -> [Constraints002,Elements002,Parts002]
  Placement = pos=(-15,-1.279e-13,1.19209e-07) rot=(0,0,1;0rad)
  Verbose = false
  _LinkVersion = 1
  _SolverType = 1
  _Version = 1
FEATURE [App::FeaturePython] Constraints002  # WARN: FeaturePython — macro-defined, semantics opaque (R4)
  Group = -> [Constraint002,Constraint023,Constraint024]
  _LinkVersion = 1
  _Version = 1
FEATURE [App::FeaturePython] Elements002  # WARN: FeaturePython — macro-defined, semantics opaque (R4)
  Group = -> [Element002,Element003,_Element032,_Element033,_Element034,_Element035]
  _LinkVersion = 1
FEATURE [Part::FeaturePython] Element002  label="BF-top-mate"  # link proxy (typed FeaturePython)
  Detach = false
  LinkTransform = true
  LinkedObject = -> Link002 [Hole001.Edge16]
  _LinkVersion = 1
  _Parent = -> Elements002
FEATURE [Part::FeaturePython] Element003  label="beam-bottom-mate"  # link proxy (typed FeaturePython)
  Detach = false
  LinkTransform = true
  LinkedObject = -> Link002 [Hole001.Edge30]
  _LinkVersion = 1
  _Parent = -> Elements002
FEATURE [App::FeaturePython] Constraint002  label="Locked002"  # WARN: FeaturePython — macro-defined, semantics opaque (R4)
  Disabled = false
  Group = -> [ElementLink002]
  _ConstraintType = 0
  _LinkVersion = 1
  _Parent = -> Constraints002
FEATURE [App::FeaturePython] ElementLink002  label="beam-bottom-mate"  # link proxy (typed FeaturePython)
  LinkTransform = true
  LinkedObject = -> Element003
  _LinkVersion = 1
  _Parent = -> Constraint002
FEATURE [Part::FeaturePython] Assembly003  label="BF12R Assembly"  # WARN: FeaturePython — macro-defined, semantics opaque (R4)
  AutoRelax = true
  BuildShape = 0
  Freeze = false
  Group = -> [Constraints003,Elements003,Parts003]
  Verbose = false
  _LinkVersion = 1
  _SolverType = 1
  _Version = 1
FEATURE [App::FeaturePython] Constraints003  # WARN: FeaturePython — macro-defined, semantics opaque (R4)
  Group = -> [Constraint003,Constraint029,Constraint030]
  _LinkVersion = 1
  _Version = 1
FEATURE [App::FeaturePython] Elements003  # WARN: FeaturePython — macro-defined, semantics opaque (R4)
  Group = -> [Element004,Element005,_Element044,_Element045,_Element046,_Element047]
  _LinkVersion = 1
FEATURE [Part::FeaturePython] Element004  label="BF-top-mate"  # link proxy (typed FeaturePython)
  Detach = false
  LinkTransform = true
  LinkedObject = -> Link003 [Hole.Edge32]
  _LinkVersion = 1
  _Parent = -> Elements003
FEATURE [Part::FeaturePython] Element005  label="beam-bottom-mate"  # link proxy (typed FeaturePython)
  Detach = false
  LinkTransform = true
  LinkedObject = -> Link003 [Hole.Edge16]
  _LinkVersion = 1
  _Parent = -> Elements003
FEATURE [App::FeaturePython] Constraint003  label="Locked003"  # WARN: FeaturePython — macro-defined, semantics opaque (R4)
  Disabled = false
  Group = -> [ElementLink003]
  _ConstraintType = 0
  _LinkVersion = 1
  _Parent = -> Constraints003
FEATURE [App::FeaturePython] ElementLink003  label="beam-bottom-mate"  # link proxy (typed FeaturePython)
  LinkTransform = true
  LinkedObject = -> Element005
  _LinkVersion = 1
  _Parent = -> Constraint003
FEATURE [Part::FeaturePython] Assembly004  label="Motor plate R Assembly"  # WARN: FeaturePython — macro-defined, semantics opaque (R4)
  AutoRelax = true
  BuildShape = 0
  Freeze = false
  Group = -> [Constraints004,Elements004,Parts004]
  Placement = pos=(0,-45,0) rot=(0,0,1;0rad)
  Verbose = false
  _LinkVersion = 1
  _SolverType = 1
  _Version = 1
FEATURE [App::FeaturePython] Constraints004  # WARN: FeaturePython — macro-defined, semantics opaque (R4)
  Group = -> [Constraint005,Constraint007,Constraint008,Constraint009,Constraint010,Constraint011,Constraint012,Constraint013,Constraint014]
  _LinkVersion = 1
  _Version = 1
FEATURE [App::FeaturePython] Elements004  # WARN: FeaturePython — macro-defined, semantics opaque (R4)
  Group = -> [Element006,_Element,_Element001,_Element002,_Element003,_Element004,_Element005,_Element006,_Element007,_Element008,_Element009,_Element010,_Element011,_Element012,_Element013,_Element014,_Element015,Element010]
  _LinkVersion = 1
FEATURE [Part::FeaturePython] Assembly005  label="Motor plate L Assembly"  # WARN: FeaturePython — macro-defined, semantics opaque (R4)
  AutoRelax = true
  BuildShape = 0
  Freeze = false
  Group = -> [Constraints005,Elements005,Parts005]
  Placement = pos=(135,-44,0) rot=(0,0,1;0rad)
  Verbose = false
  _LinkVersion = 1
  _SolverType = 1
  _Version = 1
FEATURE [App::FeaturePython] Constraints005  # WARN: FeaturePython — macro-defined, semantics opaque (R4)
  Group = -> [Constraint006,Constraint015,Constraint016,Constraint017,Constraint018,Constraint019,Constraint020,Constraint021,Constraint022]
  _LinkVersion = 1
  _Version = 1
FEATURE [App::FeaturePython] Elements005  # WARN: FeaturePython — macro-defined, semantics opaque (R4)
  Group = -> [Element007,_Element016,_Element017,_Element018,_Element019,_Element020,_Element021,_Element022,_Element023,_Element024,_Element025,_Element026,_Element027,_Element028,_Element029,_Element030,_Element031,Element011]
  _LinkVersion = 1
FEATURE [Part::FeaturePython] Element006  label="motor mate"  # link proxy (typed FeaturePython)
  Detach = false
  LinkTransform = true
  LinkedObject = -> Link004 [Fillet.Edge34]
  _LinkVersion = 1
  _Parent = -> Elements004
FEATURE [App::FeaturePython] Constraint005  label="Locked005"  # WARN: FeaturePython — macro-defined, semantics opaque (R4)
  Disabled = false
  Group = -> [ElementLink005]
  _ConstraintType = 0
  _LinkVersion = 1
  _Parent = -> Constraints004
FEATURE [App::FeaturePython] ElementLink005  label="motor mate"  # link proxy (typed FeaturePython)
  LinkTransform = true
  LinkedObject = -> Element006
  _LinkVersion = 1
  _Parent = -> Constraint005
FEATURE [Part::FeaturePython] Element007  label="motor mate"  # link proxy (typed FeaturePython)
  Detach = false
  LinkTransform = true
  LinkedObject = -> Link006 [Fillet.Edge12]
  _LinkVersion = 1
  _Parent = -> Elements005
FEATURE [App::FeaturePython] Constraint006  label="Locked006"  # WARN: FeaturePython — macro-defined, semantics opaque (R4)
  Disabled = false
  Group = -> [ElementLink006]
  _ConstraintType = 0
  _LinkVersion = 1
  _Parent = -> Constraints005
FEATURE [App::FeaturePython] ElementLink006  label="motor mate"  # link proxy (typed FeaturePython)
  LinkTransform = true
  LinkedObject = -> Element007
  _LinkVersion = 1
  _Parent = -> Constraint006
FEATURE [App::FeaturePython] Constraint007  label="Attachment"  # WARN: FeaturePython — macro-defined, semantics opaque (R4)
  Cascade = false
  Disabled = false
  Group = -> [ElementLink007,ElementLink008]
  Multiply = false
  _ConstraintType = 45
  _LinkVersion = 1
  _Parent = -> Constraints004
FEATURE [App::FeaturePython] ElementLink007  label="_Element"  # link proxy (typed FeaturePython)
  LinkTransform = true
  LinkedObject = -> _Element
  _LinkVersion = 1
  _Parent = -> Constraint007
FEATURE [Part::FeaturePython] _Element  # link proxy (typed FeaturePython)
  Detach = false
  LinkTransform = true
  LinkedObject = -> Link007 [0.Edge4]
  _LinkVersion = 1
  _Parent = -> Elements004
FEATURE [App::FeaturePython] ElementLink008  label="_Element001"  # link proxy (typed FeaturePython)
  LinkTransform = true
  LinkedObject = -> _Element001
  _LinkVersion = 1
  _Parent = -> Constraint007
FEATURE [Part::FeaturePython] _Element001  # link proxy (typed FeaturePython)
  Detach = false
  LinkTransform = true
  LinkedObject = -> Link004 [Fillet.Edge42]
  _LinkVersion = 1
  _Parent = -> Elements004
FEATURE [App::FeaturePython] Constraint008  label="Attachment001"  # WARN: FeaturePython — macro-defined, semantics opaque (R4)
  Cascade = false
  Disabled = false
  Group = -> [ElementLink009,ElementLink010]
  Multiply = false
  _ConstraintType = 45
  _LinkVersion = 1
  _Parent = -> Constraints004
FEATURE [App::FeaturePython] ElementLink009  label="_Element002"  # link proxy (typed FeaturePython)
  LinkTransform = true
  LinkedObject = -> _Element002
  _LinkVersion = 1
  _Parent = -> Constraint008
FEATURE [Part::FeaturePython] _Element002  # link proxy (typed FeaturePython)
  Detach = false
  LinkTransform = true
  LinkedObject = -> Link007 [1.Edge4]
  _LinkVersion = 1
  _Parent = -> Elements004
FEATURE [App::FeaturePython] ElementLink010  label="_Element003"  # link proxy (typed FeaturePython)
  LinkTransform = true
  LinkedObject = -> _Element003
  _LinkVersion = 1
  _Parent = -> Constraint008
FEATURE [Part::FeaturePython] _Element003  # link proxy (typed FeaturePython)
  Detach = false
  LinkTransform = true
  LinkedObject = -> Link004 [Fillet.Edge41]
  _LinkVersion = 1
  _Parent = -> Elements004
FEATURE [App::FeaturePython] Constraint009  label="Attachment002"  # WARN: FeaturePython — macro-defined, semantics opaque (R4)
  Cascade = false
  Disabled = false
  Group = -> [ElementLink011,ElementLink012]
  Multiply = false
  _ConstraintType = 45
  _LinkVersion = 1
  _Parent = -> Constraints004
FEATURE [App::FeaturePython] ElementLink011  label="_Element004"  # link proxy (typed FeaturePython)
  LinkTransform = true
  LinkedObject = -> _Element004
  _LinkVersion = 1
  _Parent = -> Constraint009
FEATURE [Part::FeaturePython] _Element004  # link proxy (typed FeaturePython)
  Detach = false
  LinkTransform = true
  LinkedObject = -> Link007 [2.Edge4]
  _LinkVersion = 1
  _Parent = -> Elements004
FEATURE [App::FeaturePython] ElementLink012  label="_Element005"  # link proxy (typed FeaturePython)
  LinkTransform = true
  LinkedObject = -> _Element005
  _LinkVersion = 1
  _Parent = -> Constraint009
FEATURE [Part::FeaturePython] _Element005  # link proxy (typed FeaturePython)
  Detach = false
  LinkTransform = true
  LinkedObject = -> Link004 [Fillet.Edge38]
  _LinkVersion = 1
  _Parent = -> Elements004
FEATURE [App::FeaturePython] Constraint010  label="Attachment003"  # WARN: FeaturePython — macro-defined, semantics opaque (R4)
  Cascade = false
  Disabled = false
  Group = -> [ElementLink013,ElementLink014]
  Multiply = false
  _ConstraintType = 45
  _LinkVersion = 1
  _Parent = -> Constraints004
FEATURE [App::FeaturePython] ElementLink013  label="_Element006"  # link proxy (typed FeaturePython)
  LinkTransform = true
  LinkedObject = -> _Element006
  _LinkVersion = 1
  _Parent = -> Constraint010
FEATURE [Part::FeaturePython] _Element006  # link proxy (typed FeaturePython)
  Detach = false
  LinkTransform = true
  LinkedObject = -> Link007 [3.Edge4]
  _LinkVersion = 1
  _Parent = -> Elements004
FEATURE [App::FeaturePython] ElementLink014  label="_Element007"  # link proxy (typed FeaturePython)
  LinkTransform = true
  LinkedObject = -> _Element007
  _LinkVersion = 1
  _Parent = -> Constraint010
FEATURE [Part::FeaturePython] _Element007  # link proxy (typed FeaturePython)
  Detach = false
  LinkTransform = true
  LinkedObject = -> Link004 [Fillet.Edge37]
  _LinkVersion = 1
  _Parent = -> Elements004
FEATURE [App::FeaturePython] Constraint011  label="Attachment004"  # WARN: FeaturePython — macro-defined, semantics opaque (R4)
  Cascade = false
  Disabled = false
  Group = -> [ElementLink015,ElementLink016]
  Multiply = false
  _ConstraintType = 45
  _LinkVersion = 1
  _Parent = -> Constraints004
FEATURE [App::FeaturePython] ElementLink015  label="_Element008"  # link proxy (typed FeaturePython)
  LinkTransform = true
  LinkedObject = -> _Element008
  _LinkVersion = 1
  _Parent = -> Constraint011
FEATURE [Part::FeaturePython] _Element008  # link proxy (typed FeaturePython)
  Detach = false
  LinkTransform = true
  LinkedObject = -> Link007 [4.Edge4]
  _LinkVersion = 1
  _Parent = -> Elements004
FEATURE [App::FeaturePython] ElementLink016  label="_Element009"  # link proxy (typed FeaturePython)
  LinkTransform = true
  LinkedObject = -> _Element009
  _LinkVersion = 1
  _Parent = -> Constraint011
FEATURE [Part::FeaturePython] _Element009  # link proxy (typed FeaturePython)
  Detach = false
  LinkTransform = true
  LinkedObject = -> Link004 [Fillet.Edge35]
  _LinkVersion = 1
  _Parent = -> Elements004
FEATURE [App::FeaturePython] Constraint012  label="Attachment005"  # WARN: FeaturePython — macro-defined, semantics opaque (R4)
  Cascade = false
  Disabled = false
  Group = -> [ElementLink017,ElementLink018]
  Multiply = false
  _ConstraintType = 45
  _LinkVersion = 1
  _Parent = -> Constraints004
FEATURE [App::FeaturePython] ElementLink017  label="_Element010"  # link proxy (typed FeaturePython)
  LinkTransform = true
  LinkedObject = -> _Element010
  _LinkVersion = 1
  _Parent = -> Constraint012
FEATURE [Part::FeaturePython] _Element010  # link proxy (typed FeaturePython)
  Detach = false
  LinkTransform = true
  LinkedObject = -> Link007 [5.Edge4]
  _LinkVersion = 1
  _Parent = -> Elements004
FEATURE [App::FeaturePython] ElementLink018  label="_Element011"  # link proxy (typed FeaturePython)
  LinkTransform = true
  LinkedObject = -> _Element011
  _LinkVersion = 1
  _Parent = -> Constraint012
FEATURE [Part::FeaturePython] _Element011  # link proxy (typed FeaturePython)
  Detach = false
  LinkTransform = true
  LinkedObject = -> Link004 [Fillet.Edge36]
  _LinkVersion = 1
  _Parent = -> Elements004
FEATURE [App::FeaturePython] Constraint013  label="Attachment006"  # WARN: FeaturePython — macro-defined, semantics opaque (R4)
  Cascade = false
  Disabled = false
  Group = -> [ElementLink019,ElementLink020]
  Multiply = false
  _ConstraintType = 45
  _LinkVersion = 1
  _Parent = -> Constraints004
FEATURE [App::FeaturePython] ElementLink019  label="_Element012"  # link proxy (typed FeaturePython)
  LinkTransform = true
  LinkedObject = -> _Element012
  _LinkVersion = 1
  _Parent = -> Constraint013
FEATURE [Part::FeaturePython] _Element012  # link proxy (typed FeaturePython)
  Detach = false
  LinkTransform = true
  LinkedObject = -> Link007 [6.Edge4]
  _LinkVersion = 1
  _Parent = -> Elements004
FEATURE [App::FeaturePython] ElementLink020  label="_Element013"  # link proxy (typed FeaturePython)
  LinkTransform = true
  LinkedObject = -> _Element013
  _LinkVersion = 1
  _Parent = -> Constraint013
FEATURE [Part::FeaturePython] _Element013  # link proxy (typed FeaturePython)
  Detach = false
  LinkTransform = true
  LinkedObject = -> Link004 [Fillet.Edge39]
  _LinkVersion = 1
  _Parent = -> Elements004
FEATURE [App::FeaturePython] Constraint014  label="Attachment007"  # WARN: FeaturePython — macro-defined, semantics opaque (R4)
  Cascade = false
  Disabled = false
  Group = -> [ElementLink021,ElementLink022]
  Multiply = false
  _ConstraintType = 45
  _LinkVersion = 1
  _Parent = -> Constraints004
FEATURE [App::FeaturePython] ElementLink021  label="_Element014"  # link proxy (typed FeaturePython)
  LinkTransform = true
  LinkedObject = -> _Element014
  _LinkVersion = 1
  _Parent = -> Constraint014
FEATURE [Part::FeaturePython] _Element014  # link proxy (typed FeaturePython)
  Detach = false
  LinkTransform = true
  LinkedObject = -> Link007 [7.Edge4]
  _LinkVersion = 1
  _Parent = -> Elements004
FEATURE [App::FeaturePython] ElementLink022  label="_Element015"  # link proxy (typed FeaturePython)
  LinkTransform = true
  LinkedObject = -> _Element015
  _LinkVersion = 1
  _Parent = -> Constraint014
FEATURE [Part::FeaturePython] _Element015  # link proxy (typed FeaturePython)
  Detach = false
  LinkTransform = true
  LinkedObject = -> Link004 [Fillet.Edge40]
  _LinkVersion = 1
  _Parent = -> Elements004
FEATURE [App::FeaturePython] Constraint015  label="Attachment008"  # WARN: FeaturePython — macro-defined, semantics opaque (R4)
  Cascade = false
  Disabled = false
  Group = -> [ElementLink023,ElementLink024]
  Multiply = false
  _ConstraintType = 45
  _LinkVersion = 1
  _Parent = -> Constraints005
FEATURE [App::FeaturePython] ElementLink023  label="_Element016"  # link proxy (typed FeaturePython)
  LinkTransform = true
  LinkedObject = -> _Element016
  Offset = pos=(0,0,0) rot=(1,0,0;3.14159rad)
  Placement = pos=(1.22392e-06,-14,76.2) rot=(1,0,0;3.14159rad)
  _LinkVersion = 1
  _Parent = -> Constraint015
FEATURE [Part::FeaturePython] _Element016  # link proxy (typed FeaturePython)
  Detach = false
  LinkTransform = true
  LinkedObject = -> Link008 [0.Edge4]
  _LinkVersion = 1
  _Parent = -> Elements005
FEATURE [App::FeaturePython] ElementLink024  label="_Element017"  # link proxy (typed FeaturePython)
  LinkTransform = true
  LinkedObject = -> _Element017
  _LinkVersion = 1
  _Parent = -> Constraint015
FEATURE [Part::FeaturePython] _Element017  # link proxy (typed FeaturePython)
  Detach = false
  LinkTransform = true
  LinkedObject = -> Link006 [Fillet.Edge19]
  _LinkVersion = 1
  _Parent = -> Elements005
FEATURE [App::FeaturePython] Constraint016  label="Attachment009"  # WARN: FeaturePython — macro-defined, semantics opaque (R4)
  Cascade = false
  Disabled = false
  Group = -> [ElementLink025,ElementLink026]
  Multiply = false
  _ConstraintType = 45
  _LinkVersion = 1
  _Parent = -> Constraints005
FEATURE [App::FeaturePython] ElementLink025  label="_Element018"  # link proxy (typed FeaturePython)
  LinkTransform = true
  LinkedObject = -> _Element018
  Offset = pos=(0,0,0) rot=(1,0,0;3.14159rad)
  Placement = pos=(1.22392e-06,-14,76.2) rot=(1,0,0;3.14159rad)
  _LinkVersion = 1
  _Parent = -> Constraint016
FEATURE [Part::FeaturePython] _Element018  # link proxy (typed FeaturePython)
  Detach = false
  LinkTransform = true
  LinkedObject = -> Link008 [1.Edge4]
  _LinkVersion = 1
  _Parent = -> Elements005
FEATURE [App::FeaturePython] ElementLink026  label="_Element019"  # link proxy (typed FeaturePython)
  LinkTransform = true
  LinkedObject = -> _Element019
  _LinkVersion = 1
  _Parent = -> Constraint016
FEATURE [Part::FeaturePython] _Element019  # link proxy (typed FeaturePython)
  Detach = false
  LinkTransform = true
  LinkedObject = -> Link006 [Fillet.Edge20]
  _LinkVersion = 1
  _Parent = -> Elements005
FEATURE [App::FeaturePython] Constraint017  label="Attachment010"  # WARN: FeaturePython — macro-defined, semantics opaque (R4)
  Cascade = false
  Disabled = false
  Group = -> [ElementLink027,ElementLink028]
  Multiply = false
  _ConstraintType = 45
  _LinkVersion = 1
  _Parent = -> Constraints005
FEATURE [App::FeaturePython] ElementLink027  label="_Element020"  # link proxy (typed FeaturePython)
  LinkTransform = true
  LinkedObject = -> _Element020
  Offset = pos=(0,0,0) rot=(1,0,0;3.14159rad)
  Placement = pos=(1.22392e-06,-14,25.4) rot=(1,0,0;3.14159rad)
  _LinkVersion = 1
  _Parent = -> Constraint017
FEATURE [Part::FeaturePython] _Element020  # link proxy (typed FeaturePython)
  Detach = false
  LinkTransform = true
  LinkedObject = -> Link008 [2.Edge4]
  _LinkVersion = 1
  _Parent = -> Elements005
FEATURE [App::FeaturePython] ElementLink028  label="_Element021"  # link proxy (typed FeaturePython)
  LinkTransform = true
  LinkedObject = -> _Element021
  _LinkVersion = 1
  _Parent = -> Constraint017
FEATURE [Part::FeaturePython] _Element021  # link proxy (typed FeaturePython)
  Detach = false
  LinkTransform = true
  LinkedObject = -> Link006 [Fillet.Edge16]
  _LinkVersion = 1
  _Parent = -> Elements005
FEATURE [App::FeaturePython] Constraint018  label="Attachment011"  # WARN: FeaturePython — macro-defined, semantics opaque (R4)
  Cascade = false
  Disabled = false
  Group = -> [ElementLink029,ElementLink030]
  Multiply = false
  _ConstraintType = 45
  _LinkVersion = 1
  _Parent = -> Constraints005
FEATURE [App::FeaturePython] ElementLink029  label="_Element022"  # link proxy (typed FeaturePython)
  LinkTransform = true
  LinkedObject = -> _Element022
  Offset = pos=(0,0,0) rot=(1,0,0;3.14159rad)
  Placement = pos=(1.22392e-06,-14,25.4) rot=(1,0,0;3.14159rad)
  _LinkVersion = 1
  _Parent = -> Constraint018
FEATURE [Part::FeaturePython] _Element022  # link proxy (typed FeaturePython)
  Detach = false
  LinkTransform = true
  LinkedObject = -> Link008 [3.Edge4]
  _LinkVersion = 1
  _Parent = -> Elements005
FEATURE [App::FeaturePython] ElementLink030  label="_Element023"  # link proxy (typed FeaturePython)
  LinkTransform = true
  LinkedObject = -> _Element023
  _LinkVersion = 1
  _Parent = -> Constraint018
FEATURE [Part::FeaturePython] _Element023  # link proxy (typed FeaturePython)
  Detach = false
  LinkTransform = true
  LinkedObject = -> Link006 [Fillet.Edge15]
  _LinkVersion = 1
  _Parent = -> Elements005
FEATURE [App::FeaturePython] Constraint019  label="Attachment012"  # WARN: FeaturePython — macro-defined, semantics opaque (R4)
  Cascade = false
  Disabled = false
  Group = -> [ElementLink031,ElementLink032]
  Multiply = false
  _ConstraintType = 45
  _LinkVersion = 1
  _Parent = -> Constraints005
FEATURE [App::FeaturePython] ElementLink031  label="_Element024"  # link proxy (typed FeaturePython)
  LinkTransform = true
  LinkedObject = -> _Element024
  Offset = pos=(0,0,0) rot=(1,0,0;3.14159rad)
  Placement = pos=(1.22392e-06,-14,-25.4) rot=(1,0,0;3.14159rad)
  _LinkVersion = 1
  _Parent = -> Constraint019
FEATURE [Part::FeaturePython] _Element024  # link proxy (typed FeaturePython)
  Detach = false
  LinkTransform = true
  LinkedObject = -> Link008 [4.Edge4]
  _LinkVersion = 1
  _Parent = -> Elements005
FEATURE [App::FeaturePython] ElementLink032  label="_Element025"  # link proxy (typed FeaturePython)
  LinkTransform = true
  LinkedObject = -> _Element025
  _LinkVersion = 1
  _Parent = -> Constraint019
FEATURE [Part::FeaturePython] _Element025  # link proxy (typed FeaturePython)
  Detach = false
  LinkTransform = true
  LinkedObject = -> Link006 [Fillet.Edge14]
  _LinkVersion = 1
  _Parent = -> Elements005
FEATURE [App::FeaturePython] Constraint020  label="Attachment013"  # WARN: FeaturePython — macro-defined, semantics opaque (R4)
  Cascade = false
  Disabled = false
  Group = -> [ElementLink033,ElementLink034]
  Multiply = false
  _ConstraintType = 45
  _LinkVersion = 1
  _Parent = -> Constraints005
FEATURE [App::FeaturePython] ElementLink033  label="_Element026"  # link proxy (typed FeaturePython)
  LinkTransform = true
  LinkedObject = -> _Element026
  Offset = pos=(0,0,0) rot=(1,0,0;3.14159rad)
  Placement = pos=(1.22392e-06,-14,-25.4) rot=(1,0,0;3.14159rad)
  _LinkVersion = 1
  _Parent = -> Constraint020
FEATURE [Part::FeaturePython] _Element026  # link proxy (typed FeaturePython)
  Detach = false
  LinkTransform = true
  LinkedObject = -> Link008 [5.Edge4]
  _LinkVersion = 1
  _Parent = -> Elements005
FEATURE [App::FeaturePython] ElementLink034  label="_Element027"  # link proxy (typed FeaturePython)
  LinkTransform = true
  LinkedObject = -> _Element027
  _LinkVersion = 1
  _Parent = -> Constraint020
FEATURE [Part::FeaturePython] _Element027  # link proxy (typed FeaturePython)
  Detach = false
  LinkTransform = true
  LinkedObject = -> Link006 [Fillet.Edge13]
  _LinkVersion = 1
  _Parent = -> Elements005
FEATURE [App::FeaturePython] Constraint021  label="Attachment014"  # WARN: FeaturePython — macro-defined, semantics opaque (R4)
  Cascade = false
  Disabled = false
  Group = -> [ElementLink035,ElementLink036]
  Multiply = false
  _ConstraintType = 45
  _LinkVersion = 1
  _Parent = -> Constraints005
FEATURE [App::FeaturePython] ElementLink035  label="_Element028"  # link proxy (typed FeaturePython)
  LinkTransform = true
  LinkedObject = -> _Element028
  Offset = pos=(0,0,0) rot=(1,0,0;3.14159rad)
  Placement = pos=(1.22392e-06,-14,-76.2) rot=(1,0,0;3.14159rad)
  _LinkVersion = 1
  _Parent = -> Constraint021
FEATURE [Part::FeaturePython] _Element028  # link proxy (typed FeaturePython)
  Detach = false
  LinkTransform = true
  LinkedObject = -> Link008 [6.Edge4]
  _LinkVersion = 1
  _Parent = -> Elements005
FEATURE [App::FeaturePython] ElementLink036  label="_Element029"  # link proxy (typed FeaturePython)
  LinkTransform = true
  LinkedObject = -> _Element029
  _LinkVersion = 1
  _Parent = -> Constraint021
FEATURE [Part::FeaturePython] _Element029  # link proxy (typed FeaturePython)
  Detach = false
  LinkTransform = true
  LinkedObject = -> Link006 [Fillet.Edge18]
  _LinkVersion = 1
  _Parent = -> Elements005
FEATURE [App::FeaturePython] Constraint022  label="Attachment015"  # WARN: FeaturePython — macro-defined, semantics opaque (R4)
  Cascade = false
  Disabled = false
  Group = -> [ElementLink037,ElementLink038]
  Multiply = false
  _ConstraintType = 45
  _LinkVersion = 1
  _Parent = -> Constraints005
FEATURE [App::FeaturePython] ElementLink037  label="_Element030"  # link proxy (typed FeaturePython)
  LinkTransform = true
  LinkedObject = -> _Element030
  Offset = pos=(0,0,0) rot=(1,0,0;3.14159rad)
  Placement = pos=(1.22392e-06,-14,-76.2) rot=(1,0,0;3.14159rad)
  _LinkVersion = 1
  _Parent = -> Constraint022
FEATURE [Part::FeaturePython] _Element030  # link proxy (typed FeaturePython)
  Detach = false
  LinkTransform = true
  LinkedObject = -> Link008 [7.Edge4]
  _LinkVersion = 1
  _Parent = -> Elements005
FEATURE [App::FeaturePython] ElementLink038  label="_Element031"  # link proxy (typed FeaturePython)
  LinkTransform = true
  LinkedObject = -> _Element031
  _LinkVersion = 1
  _Parent = -> Constraint022
FEATURE [Part::FeaturePython] _Element031  # link proxy (typed FeaturePython)
  Detach = false
  LinkTransform = true
  LinkedObject = -> Link006 [Fillet.Edge17]
  _LinkVersion = 1
  _Parent = -> Elements005
FEATURE [App::FeaturePython] Constraint023  label="Attachment016"  # WARN: FeaturePython — macro-defined, semantics opaque (R4)
  Cascade = false
  Disabled = false
  Group = -> [ElementLink039,ElementLink040]
  Multiply = false
  _ConstraintType = 45
  _LinkVersion = 1
  _Parent = -> Constraints002
FEATURE [App::FeaturePython] ElementLink039  label="_Element032"  # link proxy (typed FeaturePython)
  LinkTransform = true
  LinkedObject = -> _Element032
  _LinkVersion = 1
  _Parent = -> Constraint023
FEATURE [Part::FeaturePython] _Element032  # link proxy (typed FeaturePython)
  Detach = false
  LinkTransform = true
  LinkedObject = -> Link009 [Link009_i0.Edge2]
  _LinkVersion = 1
  _Parent = -> Elements002
FEATURE [App::FeaturePython] ElementLink040  label="_Element033"  # link proxy (typed FeaturePython)
  LinkTransform = true
  LinkedObject = -> _Element033
  _LinkVersion = 1
  _Parent = -> Constraint023
FEATURE [Part::FeaturePython] _Element033  # link proxy (typed FeaturePython)
  Detach = false
  LinkTransform = true
  LinkedObject = -> Link002 [Hole001.Edge9]
  _LinkVersion = 1
  _Parent = -> Elements002
FEATURE [App::FeaturePython] Constraint024  label="Attachment017"  # WARN: FeaturePython — macro-defined, semantics opaque (R4)
  Cascade = false
  Disabled = false
  Group = -> [ElementLink041,ElementLink042]
  Multiply = false
  _ConstraintType = 45
  _LinkVersion = 1
  _Parent = -> Constraints002
FEATURE [App::FeaturePython] ElementLink041  label="_Element034"  # link proxy (typed FeaturePython)
  LinkTransform = true
  LinkedObject = -> _Element034
  _LinkVersion = 1
  _Parent = -> Constraint024
FEATURE [Part::FeaturePython] _Element034  # link proxy (typed FeaturePython)
  Detach = false
  LinkTransform = true
  LinkedObject = -> Link009 [1.Edge2]
  _LinkVersion = 1
  _Parent = -> Elements002
FEATURE [App::FeaturePython] ElementLink042  label="_Element035"  # link proxy (typed FeaturePython)
  LinkTransform = true
  LinkedObject = -> _Element035
  _LinkVersion = 1
  _Parent = -> Constraint024
FEATURE [Part::FeaturePython] _Element035  # link proxy (typed FeaturePython)
  Detach = false
  LinkTransform = true
  LinkedObject = -> Link002 [Hole001.Edge14]
  _LinkVersion = 1
  _Parent = -> Elements002
FEATURE [App::FeaturePython] Constraint025  label="Attachment018"  # WARN: FeaturePython — macro-defined, semantics opaque (R4)
  Cascade = false
  Disabled = false
  Group = -> [ElementLink043,ElementLink044]
  Multiply = false
  _ConstraintType = 45
  _LinkVersion = 1
  _Parent = -> Constraints001
FEATURE [App::FeaturePython] ElementLink043  label="_Element036"  # link proxy (typed FeaturePython)
  LinkTransform = true
  LinkedObject = -> _Element036
  _LinkVersion = 1
  _Parent = -> Constraint025
FEATURE [Part::FeaturePython] _Element036  # link proxy (typed FeaturePython)
  Detach = false
  LinkTransform = true
  LinkedObject = -> Link010 [3.Edge2]
  _LinkVersion = 1
  _Parent = -> Elements001
FEATURE [App::FeaturePython] ElementLink044  label="_Element037"  # link proxy (typed FeaturePython)
  LinkTransform = true
  LinkedObject = -> _Element037
  _LinkVersion = 1
  _Parent = -> Constraint025
FEATURE [Part::FeaturePython] _Element037  # link proxy (typed FeaturePython)
  Detach = false
  LinkTransform = true
  LinkedObject = -> Link001 [Hole003.Edge20]
  _LinkVersion = 1
  _Parent = -> Elements001
FEATURE [App::FeaturePython] Constraint026  label="Attachment019"  # WARN: FeaturePython — macro-defined, semantics opaque (R4)
  Cascade = false
  Disabled = false
  Group = -> [ElementLink045,ElementLink046]
  Multiply = false
  _ConstraintType = 45
  _LinkVersion = 1
  _Parent = -> Constraints001
FEATURE [App::FeaturePython] ElementLink045  label="_Element038"  # link proxy (typed FeaturePython)
  LinkTransform = true
  LinkedObject = -> _Element038
  _LinkVersion = 1
  _Parent = -> Constraint026
FEATURE [Part::FeaturePython] _Element038  # link proxy (typed FeaturePython)
  Detach = false
  LinkTransform = true
  LinkedObject = -> Link010 [2.Edge2]
  _LinkVersion = 1
  _Parent = -> Elements001
FEATURE [App::FeaturePython] ElementLink046  label="_Element039"  # link proxy (typed FeaturePython)
  LinkTransform = true
  LinkedObject = -> _Element039
  _LinkVersion = 1
  _Parent = -> Constraint026
FEATURE [Part::FeaturePython] _Element039  # link proxy (typed FeaturePython)
  Detach = false
  LinkTransform = true
  LinkedObject = -> Link001 [Hole003.Edge11]
  _LinkVersion = 1
  _Parent = -> Elements001
FEATURE [App::FeaturePython] Constraint027  label="Attachment020"  # WARN: FeaturePython — macro-defined, semantics opaque (R4)
  Cascade = false
  Disabled = false
  Group = -> [ElementLink047,ElementLink048]
  Multiply = false
  _ConstraintType = 45
  _LinkVersion = 1
  _Parent = -> Constraints001
FEATURE [App::FeaturePython] ElementLink047  label="_Element040"  # link proxy (typed FeaturePython)
  LinkTransform = true
  LinkedObject = -> _Element040
  _LinkVersion = 1
  _Parent = -> Constraint027
FEATURE [Part::FeaturePython] _Element040  # link proxy (typed FeaturePython)
  Detach = false
  LinkTransform = true
  LinkedObject = -> Link010 [1.Edge2]
  _LinkVersion = 1
  _Parent = -> Elements001
FEATURE [App::FeaturePython] ElementLink048  label="_Element041"  # link proxy (typed FeaturePython)
  LinkTransform = true
  LinkedObject = -> _Element041
  _LinkVersion = 1
  _Parent = -> Constraint027
FEATURE [Part::FeaturePython] _Element041  # link proxy (typed FeaturePython)
  Detach = false
  LinkTransform = true
  LinkedObject = -> Link001 [Hole003.Edge24]
  _LinkVersion = 1
  _Parent = -> Elements001
FEATURE [App::FeaturePython] Constraint028  label="Attachment021"  # WARN: FeaturePython — macro-defined, semantics opaque (R4)
  Cascade = false
  Disabled = false
  Group = -> [ElementLink049,ElementLink050]
  Multiply = false
  _ConstraintType = 45
  _LinkVersion = 1
  _Parent = -> Constraints001
FEATURE [App::FeaturePython] ElementLink049  label="_Element042"  # link proxy (typed FeaturePython)
  LinkTransform = true
  LinkedObject = -> _Element042
  _LinkVersion = 1
  _Parent = -> Constraint028
FEATURE [Part::FeaturePython] _Element042  # link proxy (typed FeaturePython)
  Detach = false
  LinkTransform = true
  LinkedObject = -> Link010 [0.Edge2]
  _LinkVersion = 1
  _Parent = -> Elements001
FEATURE [App::FeaturePython] ElementLink050  label="_Element043"  # link proxy (typed FeaturePython)
  LinkTransform = true
  LinkedObject = -> _Element043
  _LinkVersion = 1
  _Parent = -> Constraint028
FEATURE [Part::FeaturePython] _Element043  # link proxy (typed FeaturePython)
  Detach = false
  LinkTransform = true
  LinkedObject = -> Link001 [Hole003.Edge12]
  _LinkVersion = 1
  _Parent = -> Elements001
FEATURE [App::FeaturePython] Constraint029  label="Attachment022"  # WARN: FeaturePython — macro-defined, semantics opaque (R4)
  Cascade = false
  Disabled = false
  Group = -> [ElementLink051,ElementLink052]
  Multiply = false
  _ConstraintType = 45
  _LinkVersion = 1
  _Parent = -> Constraints003
FEATURE [App::FeaturePython] ElementLink051  label="_Element044"  # link proxy (typed FeaturePython)
  LinkTransform = true
  LinkedObject = -> _Element044
  _LinkVersion = 1
  _Parent = -> Constraint029
FEATURE [Part::FeaturePython] _Element044  # link proxy (typed FeaturePython)
  Detach = false
  LinkTransform = true
  LinkedObject = -> Link011 [0.Edge2]
  _LinkVersion = 1
  _Parent = -> Elements003
FEATURE [App::FeaturePython] ElementLink052  label="_Element045"  # link proxy (typed FeaturePython)
  LinkTransform = true
  LinkedObject = -> _Element045
  _LinkVersion = 1
  _Parent = -> Constraint029
FEATURE [Part::FeaturePython] _Element045  # link proxy (typed FeaturePython)
  Detach = false
  LinkTransform = true
  LinkedObject = -> Link003 [Hole.Edge26]
  _LinkVersion = 1
  _Parent = -> Elements003
FEATURE [App::FeaturePython] Constraint030  label="Attachment023"  # WARN: FeaturePython — macro-defined, semantics opaque (R4)
  Cascade = false
  Disabled = false
  Group = -> [ElementLink053,ElementLink054]
  Multiply = false
  _ConstraintType = 45
  _LinkVersion = 1
  _Parent = -> Constraints003
FEATURE [App::FeaturePython] ElementLink053  label="_Element046"  # link proxy (typed FeaturePython)
  LinkTransform = true
  LinkedObject = -> _Element046
  _LinkVersion = 1
  _Parent = -> Constraint030
FEATURE [Part::FeaturePython] _Element046  # link proxy (typed FeaturePython)
  Detach = false
  LinkTransform = true
  LinkedObject = -> Link003 [Hole.Edge30]
  _LinkVersion = 1
  _Parent = -> Elements003
FEATURE [App::FeaturePython] ElementLink054  label="_Element047"  # link proxy (typed FeaturePython)
  LinkTransform = true
  LinkedObject = -> _Element047
  _LinkVersion = 1
  _Parent = -> Constraint030
FEATURE [Part::FeaturePython] _Element047  # link proxy (typed FeaturePython)
  Detach = false
  LinkTransform = true
  LinkedObject = -> Link011 [1.Edge2]
  _LinkVersion = 1
  _Parent = -> Elements003
FEATURE [App::FeaturePython] Constraint031  label="Attachment024"  # WARN: FeaturePython — macro-defined, semantics opaque (R4)
  Cascade = false
  Disabled = false
  Group = -> [ElementLink055,ElementLink056]
  Multiply = false
  _ConstraintType = 45
  _LinkVersion = 1
  _Parent = -> Constraints
FEATURE [App::FeaturePython] ElementLink055  label="_Element048"  # link proxy (typed FeaturePython)
  LinkTransform = true
  LinkedObject = -> _Element048
  _LinkVersion = 1
  _Parent = -> Constraint031
FEATURE [Part::FeaturePython] _Element048  # link proxy (typed FeaturePython)
  Detach = false
  LinkTransform = true
  LinkedObject = -> Link012 [0.Edge2]
  _LinkVersion = 1
  _Parent = -> Elements
FEATURE [App::FeaturePython] ElementLink056  label="_Element049"  # link proxy (typed FeaturePython)
  LinkTransform = true
  LinkedObject = -> _Element049
  _LinkVersion = 1
  _Parent = -> Constraint031
FEATURE [Part::FeaturePython] _Element049  # link proxy (typed FeaturePython)
  Detach = false
  LinkTransform = true
  LinkedObject = -> Link [Hole002.?Edge40]
  _LinkVersion = 1
  _Parent = -> Elements
FEATURE [App::FeaturePython] Constraint032  label="Attachment025"  # WARN: FeaturePython — macro-defined, semantics opaque (R4)
  Cascade = false
  Disabled = false
  Group = -> [ElementLink057,ElementLink058]
  Multiply = false
  _ConstraintType = 45
  _LinkVersion = 1
  _Parent = -> Constraints
FEATURE [App::FeaturePython] ElementLink057  label="_Element050"  # link proxy (typed FeaturePython)
  LinkTransform = true
  LinkedObject = -> _Element050
  _LinkVersion = 1
  _Parent = -> Constraint032
FEATURE [Part::FeaturePython] _Element050  # link proxy (typed FeaturePython)
  Detach = false
  LinkTransform = true
  LinkedObject = -> Link012 [1.Edge2]
  _LinkVersion = 1
  _Parent = -> Elements
FEATURE [App::FeaturePython] ElementLink058  label="_Element051"  # link proxy (typed FeaturePython)
  LinkTransform = true
  LinkedObject = -> _Element051
  _LinkVersion = 1
  _Parent = -> Constraint032
FEATURE [Part::FeaturePython] _Element051  # link proxy (typed FeaturePython)
  Detach = false
  LinkTransform = true
  LinkedObject = -> Link [Hole002.Edge31]
  _LinkVersion = 1
  _Parent = -> Elements
FEATURE [App::FeaturePython] Constraint033  label="Attachment026"  # WARN: FeaturePython — macro-defined, semantics opaque (R4)
  Cascade = false
  Disabled = false
  Group = -> [ElementLink059,ElementLink060]
  Multiply = false
  _ConstraintType = 45
  _LinkVersion = 1
  _Parent = -> Constraints
FEATURE [App::FeaturePython] ElementLink059  label="_Element052"  # link proxy (typed FeaturePython)
  LinkTransform = true
  LinkedObject = -> _Element052
  _LinkVersion = 1
  _Parent = -> Constraint033
FEATURE [Part::FeaturePython] _Element052  # link proxy (typed FeaturePython)
  Detach = false
  LinkTransform = true
  LinkedObject = -> Link012 [2.Edge2]
  _LinkVersion = 1
  _Parent = -> Elements
FEATURE [App::FeaturePython] ElementLink060  label="_Element053"  # link proxy (typed FeaturePython)
  LinkTransform = true
  LinkedObject = -> _Element053
  _LinkVersion = 1
  _Parent = -> Constraint033
FEATURE [Part::FeaturePython] _Element053  # link proxy (typed FeaturePython)
  Detach = false
  LinkTransform = true
  LinkedObject = -> Link [Hole002.Edge44]
  _LinkVersion = 1
  _Parent = -> Elements
FEATURE [App::FeaturePython] Constraint034  label="Attachment027"  # WARN: FeaturePython — macro-defined, semantics opaque (R4)
  Cascade = false
  Disabled = false
  Group = -> [ElementLink061,ElementLink062]
  Multiply = false
  _ConstraintType = 45
  _LinkVersion = 1
  _Parent = -> Constraints
FEATURE [App::FeaturePython] ElementLink061  label="_Element054"  # link proxy (typed FeaturePython)
  LinkTransform = true
  LinkedObject = -> _Element054
  _LinkVersion = 1
  _Parent = -> Constraint034
FEATURE [Part::FeaturePython] _Element054  # link proxy (typed FeaturePython)
  Detach = false
  LinkTransform = true
  LinkedObject = -> Link012 [3.Edge2]
  _LinkVersion = 1
  _Parent = -> Elements
FEATURE [App::FeaturePython] ElementLink062  label="_Element055"  # link proxy (typed FeaturePython)
  LinkTransform = true
  LinkedObject = -> _Element055
  _LinkVersion = 1
  _Parent = -> Constraint034
FEATURE [Part::FeaturePython] _Element055  # link proxy (typed FeaturePython)
  Detach = false
  LinkTransform = true
  LinkedObject = -> Link [Hole002.Edge32]
  _LinkVersion = 1
  _Parent = -> Elements
FEATURE [Part::FeaturePython] Assembly006  label="Front plate Assembly L"  # WARN: FeaturePython — macro-defined, semantics opaque (R4)
  AutoRelax = true
  BuildShape = 0
  Freeze = false
  Group = -> [Constraints006,Elements006,Parts006]
  Placement = pos=(220,41.65,0) rot=(0,0,1;3.14159rad)
  Verbose = false
  _LinkVersion = 1
  _SolverType = 1
  _Version = 1
FEATURE [App::FeaturePython] Constraints006  # WARN: FeaturePython — macro-defined, semantics opaque (R4)
  Group = -> [Constraint035,Constraint037,Constraint038,Constraint039,Constraint040,Constraint041,Constraint042,Constraint043,Constraint044]
  _LinkVersion = 1
  _Version = 1
FEATURE [App::FeaturePython] Elements006  # WARN: FeaturePython — macro-defined, semantics opaque (R4)
  Group = -> [_Element056,_Element058,_Element059,_Element060,_Element061,_Element062,_Element063,_Element064,_Element065,_Element066,_Element067,_Element068,_Element069,_Element070,_Element071,_Element072,_Element073,Element008]
  _LinkVersion = 1
FEATURE [Part::FeaturePython] Assembly007  label="Front plate Assemply R"  # WARN: FeaturePython — macro-defined, semantics opaque (R4)
  AutoRelax = true
  BuildShape = 0
  Freeze = false
  Group = -> [Constraints007,Elements007,Parts007]
  Placement = pos=(84,47,0) rot=(0,0,1;0rad)
  Verbose = false
  _LinkVersion = 1
  _SolverType = 1
  _Version = 1
FEATURE [App::FeaturePython] Constraints007  # WARN: FeaturePython — macro-defined, semantics opaque (R4)
  Group = -> [Constraint036,Constraint045,Constraint046,Constraint047,Constraint048,Constraint049,Constraint050,Constraint051,Constraint052]
  _LinkVersion = 1
  _Version = 1
FEATURE [App::FeaturePython] Elements007  # WARN: FeaturePython — macro-defined, semantics opaque (R4)
  Group = -> [_Element057,_Element074,_Element075,_Element076,_Element077,_Element078,_Element079,_Element080,_Element081,_Element082,_Element083,_Element084,_Element085,_Element086,_Element087,_Element088,_Element089,Element009]
  _LinkVersion = 1
FEATURE [App::FeaturePython] Constraint035  label="Locked007"  # WARN: FeaturePython — macro-defined, semantics opaque (R4)
  Disabled = false
  Group = -> [ElementLink063]
  _ConstraintType = 0
  _LinkVersion = 1
  _Parent = -> Constraints006
FEATURE [App::FeaturePython] ElementLink063  label="_Element056"  # link proxy (typed FeaturePython)
  LinkTransform = true
  LinkedObject = -> _Element056
  _LinkVersion = 1
  _Parent = -> Constraint035
FEATURE [Part::FeaturePython] _Element056  # link proxy (typed FeaturePython)
  Detach = false
  LinkTransform = true
  LinkedObject = -> Link014 [Fillet001.Face2]
  _LinkVersion = 1
  _Parent = -> Elements006
FEATURE [App::FeaturePython] Constraint036  label="Locked008"  # WARN: FeaturePython — macro-defined, semantics opaque (R4)
  Disabled = false
  Group = -> [ElementLink064]
  _ConstraintType = 0
  _LinkVersion = 1
  _Parent = -> Constraints007
FEATURE [App::FeaturePython] ElementLink064  label="_Element057"  # link proxy (typed FeaturePython)
  LinkTransform = true
  LinkedObject = -> _Element057
  _LinkVersion = 1
  _Parent = -> Constraint036
FEATURE [Part::FeaturePython] _Element057  # link proxy (typed FeaturePython)
  Detach = false
  LinkTransform = true
  LinkedObject = -> Link013 [Fillet001.Face5]
  _LinkVersion = 1
  _Parent = -> Elements007
FEATURE [App::FeaturePython] Constraint037  label="Attachment028"  # WARN: FeaturePython — macro-defined, semantics opaque (R4)
  Cascade = false
  Disabled = false
  Group = -> [ElementLink065,ElementLink066]
  Multiply = false
  _ConstraintType = 45
  _LinkVersion = 1
  _Parent = -> Constraints006
FEATURE [App::FeaturePython] ElementLink065  label="_Element058"  # link proxy (typed FeaturePython)
  LinkTransform = true
  LinkedObject = -> _Element058
  _LinkVersion = 1
  _Parent = -> Constraint037
FEATURE [Part::FeaturePython] _Element058  # link proxy (typed FeaturePython)
  Detach = false
  LinkTransform = true
  LinkedObject = -> Link014 [Fillet001.Edge31]
  _LinkVersion = 1
  _Parent = -> Elements006
FEATURE [App::FeaturePython] ElementLink066  label="_Element059"  # link proxy (typed FeaturePython)
  LinkTransform = true
  LinkedObject = -> _Element059
  _LinkVersion = 1
  _Parent = -> Constraint037
FEATURE [Part::FeaturePython] _Element059  # link proxy (typed FeaturePython)
  Detach = false
  LinkTransform = true
  LinkedObject = -> Link016 [0.Edge4]
  _LinkVersion = 1
  _Parent = -> Elements006
FEATURE [App::FeaturePython] Constraint038  label="Attachment029"  # WARN: FeaturePython — macro-defined, semantics opaque (R4)
  Cascade = false
  Disabled = false
  Group = -> [ElementLink067,ElementLink068]
  Multiply = false
  _ConstraintType = 45
  _LinkVersion = 1
  _Parent = -> Constraints006
FEATURE [App::FeaturePython] ElementLink067  label="_Element060"  # link proxy (typed FeaturePython)
  LinkTransform = true
  LinkedObject = -> _Element060
  _LinkVersion = 1
  _Parent = -> Constraint038
FEATURE [Part::FeaturePython] _Element060  # link proxy (typed FeaturePython)
  Detach = false
  LinkTransform = true
  LinkedObject = -> Link014 [Fillet001.Edge32]
  _LinkVersion = 1
  _Parent = -> Elements006
FEATURE [App::FeaturePython] ElementLink068  label="_Element061"  # link proxy (typed FeaturePython)
  LinkTransform = true
  LinkedObject = -> _Element061
  _LinkVersion = 1
  _Parent = -> Constraint038
FEATURE [Part::FeaturePython] _Element061  # link proxy (typed FeaturePython)
  Detach = false
  LinkTransform = true
  LinkedObject = -> Link016 [1.Edge4]
  _LinkVersion = 1
  _Parent = -> Elements006
FEATURE [App::FeaturePython] Constraint039  label="Attachment030"  # WARN: FeaturePython — macro-defined, semantics opaque (R4)
  Cascade = false
  Disabled = false
  Group = -> [ElementLink069,ElementLink070]
  Multiply = false
  _ConstraintType = 45
  _LinkVersion = 1
  _Parent = -> Constraints006
FEATURE [App::FeaturePython] ElementLink069  label="_Element062"  # link proxy (typed FeaturePython)
  LinkTransform = true
  LinkedObject = -> _Element062
  _LinkVersion = 1
  _Parent = -> Constraint039
FEATURE [Part::FeaturePython] _Element062  # link proxy (typed FeaturePython)
  Detach = false
  LinkTransform = true
  LinkedObject = -> Link014 [Fillet001.Edge35]
  _LinkVersion = 1
  _Parent = -> Elements006
FEATURE [App::FeaturePython] ElementLink070  label="_Element063"  # link proxy (typed FeaturePython)
  LinkTransform = true
  LinkedObject = -> _Element063
  _LinkVersion = 1
  _Parent = -> Constraint039
FEATURE [Part::FeaturePython] _Element063  # link proxy (typed FeaturePython)
  Detach = false
  LinkTransform = true
  LinkedObject = -> Link016 [2.Edge4]
  _LinkVersion = 1
  _Parent = -> Elements006
FEATURE [App::FeaturePython] Constraint040  label="Attachment031"  # WARN: FeaturePython — macro-defined, semantics opaque (R4)
  Cascade = false
  Disabled = false
  Group = -> [ElementLink071,ElementLink072]
  Multiply = false
  _ConstraintType = 45
  _LinkVersion = 1
  _Parent = -> Constraints006
FEATURE [App::FeaturePython] ElementLink071  label="_Element064"  # link proxy (typed FeaturePython)
  LinkTransform = true
  LinkedObject = -> _Element064
  _LinkVersion = 1
  _Parent = -> Constraint040
FEATURE [Part::FeaturePython] _Element064  # link proxy (typed FeaturePython)
  Detach = false
  LinkTransform = true
  LinkedObject = -> Link016 [3.Edge4]
  _LinkVersion = 1
  _Parent = -> Elements006
FEATURE [App::FeaturePython] ElementLink072  label="_Element065"  # link proxy (typed FeaturePython)
  LinkTransform = true
  LinkedObject = -> _Element065
  _LinkVersion = 1
  _Parent = -> Constraint040
FEATURE [Part::FeaturePython] _Element065  # link proxy (typed FeaturePython)
  Detach = false
  LinkTransform = true
  LinkedObject = -> Link014 [Fillet001.Edge36]
  _LinkVersion = 1
  _Parent = -> Elements006
FEATURE [App::FeaturePython] Constraint041  label="Attachment032"  # WARN: FeaturePython — macro-defined, semantics opaque (R4)
  Cascade = false
  Disabled = false
  Group = -> [ElementLink073,ElementLink074]
  Multiply = false
  _ConstraintType = 45
  _LinkVersion = 1
  _Parent = -> Constraints006
FEATURE [App::FeaturePython] ElementLink073  label="_Element066"  # link proxy (typed FeaturePython)
  LinkTransform = true
  LinkedObject = -> _Element066
  _LinkVersion = 1
  _Parent = -> Constraint041
FEATURE [Part::FeaturePython] _Element066  # link proxy (typed FeaturePython)
  Detach = false
  LinkTransform = true
  LinkedObject = -> Link016 [4.Edge4]
  _LinkVersion = 1
  _Parent = -> Elements006
FEATURE [App::FeaturePython] ElementLink074  label="_Element067"  # link proxy (typed FeaturePython)
  LinkTransform = true
  LinkedObject = -> _Element067
  _LinkVersion = 1
  _Parent = -> Constraint041
FEATURE [Part::FeaturePython] _Element067  # link proxy (typed FeaturePython)
  Detach = false
  LinkTransform = true
  LinkedObject = -> Link014 [Fillet001.Edge34]
  _LinkVersion = 1
  _Parent = -> Elements006
FEATURE [App::FeaturePython] Constraint042  label="Attachment033"  # WARN: FeaturePython — macro-defined, semantics opaque (R4)
  Cascade = false
  Disabled = false
  Group = -> [ElementLink075,ElementLink076]
  Multiply = false
  _ConstraintType = 45
  _LinkVersion = 1
  _Parent = -> Constraints006
FEATURE [App::FeaturePython] ElementLink075  label="_Element068"  # link proxy (typed FeaturePython)
  LinkTransform = true
  LinkedObject = -> _Element068
  _LinkVersion = 1
  _Parent = -> Constraint042
FEATURE [Part::FeaturePython] _Element068  # link proxy (typed FeaturePython)
  Detach = false
  LinkTransform = true
  LinkedObject = -> Link016 [5.Edge4]
  _LinkVersion = 1
  _Parent = -> Elements006
FEATURE [App::FeaturePython] ElementLink076  label="_Element069"  # link proxy (typed FeaturePython)
  LinkTransform = true
  LinkedObject = -> _Element069
  _LinkVersion = 1
  _Parent = -> Constraint042
FEATURE [Part::FeaturePython] _Element069  # link proxy (typed FeaturePython)
  Detach = false
  LinkTransform = true
  LinkedObject = -> Link014 [Fillet001.Edge33]
  _LinkVersion = 1
  _Parent = -> Elements006
FEATURE [App::FeaturePython] Constraint043  label="Attachment034"  # WARN: FeaturePython — macro-defined, semantics opaque (R4)
  Cascade = false
  Disabled = false
  Group = -> [ElementLink077,ElementLink078]
  Multiply = false
  _ConstraintType = 45
  _LinkVersion = 1
  _Parent = -> Constraints006
FEATURE [App::FeaturePython] ElementLink077  label="_Element070"  # link proxy (typed FeaturePython)
  LinkTransform = true
  LinkedObject = -> _Element070
  _LinkVersion = 1
  _Parent = -> Constraint043
FEATURE [Part::FeaturePython] _Element070  # link proxy (typed FeaturePython)
  Detach = false
  LinkTransform = true
  LinkedObject = -> Link016 [6.Edge4]
  _LinkVersion = 1
  _Parent = -> Elements006
FEATURE [App::FeaturePython] ElementLink078  label="_Element071"  # link proxy (typed FeaturePython)
  LinkTransform = true
  LinkedObject = -> _Element071
  _LinkVersion = 1
  _Parent = -> Constraint043
FEATURE [Part::FeaturePython] _Element071  # link proxy (typed FeaturePython)
  Detach = false
  LinkTransform = true
  LinkedObject = -> Link014 [Fillet001.Edge30]
  _LinkVersion = 1
  _Parent = -> Elements006
FEATURE [App::FeaturePython] Constraint044  label="Attachment035"  # WARN: FeaturePython — macro-defined, semantics opaque (R4)
  Cascade = false
  Disabled = false
  Group = -> [ElementLink079,ElementLink080]
  Multiply = false
  _ConstraintType = 45
  _LinkVersion = 1
  _Parent = -> Constraints006
FEATURE [App::FeaturePython] ElementLink079  label="_Element072"  # link proxy (typed FeaturePython)
  LinkTransform = true
  LinkedObject = -> _Element072
  _LinkVersion = 1
  _Parent = -> Constraint044
FEATURE [Part::FeaturePython] _Element072  # link proxy (typed FeaturePython)
  Detach = false
  LinkTransform = true
  LinkedObject = -> Link016 [7.Edge4]
  _LinkVersion = 1
  _Parent = -> Elements006
FEATURE [App::FeaturePython] ElementLink080  label="_Element073"  # link proxy (typed FeaturePython)
  LinkTransform = true
  LinkedObject = -> _Element073
  _LinkVersion = 1
  _Parent = -> Constraint044
FEATURE [Part::FeaturePython] _Element073  # link proxy (typed FeaturePython)
  Detach = false
  LinkTransform = true
  LinkedObject = -> Link014 [Fillet001.Edge29]
  _LinkVersion = 1
  _Parent = -> Elements006
FEATURE [App::FeaturePython] Constraint045  label="Attachment036"  # WARN: FeaturePython — macro-defined, semantics opaque (R4)
  Cascade = false
  Disabled = false
  Group = -> [ElementLink081,ElementLink082]
  Multiply = false
  _ConstraintType = 45
  _LinkVersion = 1
  _Parent = -> Constraints007
FEATURE [App::FeaturePython] ElementLink081  label="_Element074"  # link proxy (typed FeaturePython)
  LinkTransform = true
  LinkedObject = -> _Element074
  Offset = pos=(0,0,0) rot=(1,0,0;3.14159rad)
  Placement = pos=(0,1.58e-14,25.4) rot=(1,0,0;3.14159rad)
  _LinkVersion = 1
  _Parent = -> Constraint045
FEATURE [Part::FeaturePython] _Element074  # link proxy (typed FeaturePython)
  Detach = false
  LinkTransform = true
  LinkedObject = -> Link015 [7.Edge4]
  _LinkVersion = 1
  _Parent = -> Elements007
FEATURE [App::FeaturePython] ElementLink082  label="_Element075"  # link proxy (typed FeaturePython)
  LinkTransform = true
  LinkedObject = -> _Element075
  _LinkVersion = 1
  _Parent = -> Constraint045
FEATURE [Part::FeaturePython] _Element075  # link proxy (typed FeaturePython)
  Detach = false
  LinkTransform = true
  LinkedObject = -> Link013 [Fillet001.Edge15]
  _LinkVersion = 1
  _Parent = -> Elements007
FEATURE [App::FeaturePython] Constraint046  label="Attachment037"  # WARN: FeaturePython — macro-defined, semantics opaque (R4)
  Cascade = false
  Disabled = false
  Group = -> [ElementLink083,ElementLink084]
  Multiply = false
  _ConstraintType = 45
  _LinkVersion = 1
  _Parent = -> Constraints007
FEATURE [App::FeaturePython] ElementLink083  label="_Element076"  # link proxy (typed FeaturePython)
  LinkTransform = true
  LinkedObject = -> _Element076
  Offset = pos=(0,0,0) rot=(1,0,0;3.14159rad)
  Placement = pos=(0,1.85e-14,25.4) rot=(1,0,0;3.14159rad)
  _LinkVersion = 1
  _Parent = -> Constraint046
FEATURE [Part::FeaturePython] _Element076  # link proxy (typed FeaturePython)
  Detach = false
  LinkTransform = true
  LinkedObject = -> Link013 [Fillet001.Edge14]
  _LinkVersion = 1
  _Parent = -> Elements007
FEATURE [App::FeaturePython] ElementLink084  label="_Element077"  # link proxy (typed FeaturePython)
  LinkTransform = true
  LinkedObject = -> _Element077
  _LinkVersion = 1
  _Parent = -> Constraint046
FEATURE [Part::FeaturePython] _Element077  # link proxy (typed FeaturePython)
  Detach = false
  LinkTransform = true
  LinkedObject = -> Link015 [6.Edge4]
  _LinkVersion = 1
  _Parent = -> Elements007
FEATURE [App::FeaturePython] Constraint047  label="Attachment038"  # WARN: FeaturePython — macro-defined, semantics opaque (R4)
  Cascade = false
  Disabled = false
  Group = -> [ElementLink085,ElementLink086]
  Multiply = false
  _ConstraintType = 45
  _LinkVersion = 1
  _Parent = -> Constraints007
FEATURE [App::FeaturePython] ElementLink085  label="_Element078"  # link proxy (typed FeaturePython)
  LinkTransform = true
  LinkedObject = -> _Element078
  Offset = pos=(0,0,0) rot=(1,0,0;3.14159rad)
  Placement = pos=(-1.42e-14,5.44e-14,76.2) rot=(1,0,0;3.14159rad)
  _LinkVersion = 1
  _Parent = -> Constraint047
FEATURE [Part::FeaturePython] _Element078  # link proxy (typed FeaturePython)
  Detach = false
  LinkTransform = true
  LinkedObject = -> Link015 [5.Edge4]
  _LinkVersion = 1
  _Parent = -> Elements007
FEATURE [App::FeaturePython] ElementLink086  label="_Element079"  # link proxy (typed FeaturePython)
  LinkTransform = true
  LinkedObject = -> _Element079
  _LinkVersion = 1
  _Parent = -> Constraint047
FEATURE [Part::FeaturePython] _Element079  # link proxy (typed FeaturePython)
  Detach = false
  LinkTransform = true
  LinkedObject = -> Link013 [Fillet001.Edge18]
  _LinkVersion = 1
  _Parent = -> Elements007
FEATURE [App::FeaturePython] Constraint048  label="Attachment039"  # WARN: FeaturePython — macro-defined, semantics opaque (R4)
  Cascade = false
  Disabled = false
  Group = -> [ElementLink087,ElementLink088]
  Multiply = false
  _ConstraintType = 45
  _LinkVersion = 1
  _Parent = -> Constraints007
FEATURE [App::FeaturePython] ElementLink087  label="_Element080"  # link proxy (typed FeaturePython)
  LinkTransform = true
  LinkedObject = -> _Element080
  Offset = pos=(0,0,0) rot=(1,0,0;3.14159rad)
  Placement = pos=(-7.1e-15,-5.44e-14,-76.2) rot=(1,0,0;3.14159rad)
  _LinkVersion = 1
  _Parent = -> Constraint048
FEATURE [Part::FeaturePython] _Element080  # link proxy (typed FeaturePython)
  Detach = false
  LinkTransform = true
  LinkedObject = -> Link015 [4.Edge4]
  _LinkVersion = 1
  _Parent = -> Elements007
FEATURE [App::FeaturePython] ElementLink088  label="_Element081"  # link proxy (typed FeaturePython)
  LinkTransform = true
  LinkedObject = -> _Element081
  _LinkVersion = 1
  _Parent = -> Constraint048
FEATURE [Part::FeaturePython] _Element081  # link proxy (typed FeaturePython)
  Detach = false
  LinkTransform = true
  LinkedObject = -> Link013 [Fillet001.Edge17]
  _LinkVersion = 1
  _Parent = -> Elements007
FEATURE [App::FeaturePython] Constraint049  label="Attachment040"  # WARN: FeaturePython — macro-defined, semantics opaque (R4)
  Cascade = false
  Disabled = false
  Group = -> [ElementLink089,ElementLink090]
  Multiply = false
  _ConstraintType = 45
  _LinkVersion = 1
  _Parent = -> Constraints007
FEATURE [App::FeaturePython] ElementLink089  label="_Element082"  # link proxy (typed FeaturePython)
  LinkTransform = true
  LinkedObject = -> _Element082
  Offset = pos=(0,0,0) rot=(1,0,0;3.14159rad)
  Placement = pos=(0,-1.58e-14,-25.4) rot=(1,0,0;3.14159rad)
  _LinkVersion = 1
  _Parent = -> Constraint049
FEATURE [Part::FeaturePython] _Element082  # link proxy (typed FeaturePython)
  Detach = false
  LinkTransform = true
  LinkedObject = -> Link015 [3.Edge4]
  _LinkVersion = 1
  _Parent = -> Elements007
FEATURE [App::FeaturePython] ElementLink090  label="_Element083"  # link proxy (typed FeaturePython)
  LinkTransform = true
  LinkedObject = -> _Element083
  _LinkVersion = 1
  _Parent = -> Constraint049
FEATURE [Part::FeaturePython] _Element083  # link proxy (typed FeaturePython)
  Detach = false
  LinkTransform = true
  LinkedObject = -> Link013 [Fillet001.Edge13]
  _LinkVersion = 1
  _Parent = -> Elements007
FEATURE [App::FeaturePython] Constraint050  label="Attachment041"  # WARN: FeaturePython — macro-defined, semantics opaque (R4)
  Cascade = false
  Disabled = false
  Group = -> [ElementLink091,ElementLink092]
  Multiply = false
  _ConstraintType = 45
  _LinkVersion = 1
  _Parent = -> Constraints007
FEATURE [App::FeaturePython] ElementLink091  label="_Element084"  # link proxy (typed FeaturePython)
  LinkTransform = true
  LinkedObject = -> _Element084
  Offset = pos=(0,0,0) rot=(1,0,0;3.14159rad)
  Placement = pos=(0,-1.58e-14,-25.4) rot=(1,0,0;3.14159rad)
  _LinkVersion = 1
  _Parent = -> Constraint050
FEATURE [Part::FeaturePython] _Element084  # link proxy (typed FeaturePython)
  Detach = false
  LinkTransform = true
  LinkedObject = -> Link015 [2.Edge4]
  _LinkVersion = 1
  _Parent = -> Elements007
FEATURE [App::FeaturePython] ElementLink092  label="_Element085"  # link proxy (typed FeaturePython)
  LinkTransform = true
  LinkedObject = -> _Element085
  _LinkVersion = 1
  _Parent = -> Constraint050
FEATURE [Part::FeaturePython] _Element085  # link proxy (typed FeaturePython)
  Detach = false
  LinkTransform = true
  LinkedObject = -> Link013 [Fillet001.Edge12]
  _LinkVersion = 1
  _Parent = -> Elements007
FEATURE [App::FeaturePython] Constraint051  label="Attachment042"  # WARN: FeaturePython — macro-defined, semantics opaque (R4)
  Cascade = false
  Disabled = false
  Group = -> [ElementLink093,ElementLink094]
  Multiply = false
  _ConstraintType = 45
  _LinkVersion = 1
  _Parent = -> Constraints007
FEATURE [App::FeaturePython] ElementLink093  label="_Element086"  # link proxy (typed FeaturePython)
  LinkTransform = true
  LinkedObject = -> _Element086
  Offset = pos=(0,0,0) rot=(1,0,0;3.14159rad)
  Placement = pos=(1.42e-14,5.44e-14,76.2) rot=(1,0,0;3.14159rad)
  _LinkVersion = 1
  _Parent = -> Constraint051
FEATURE [Part::FeaturePython] _Element086  # link proxy (typed FeaturePython)
  Detach = false
  LinkTransform = true
  LinkedObject = -> Link015 [0.Edge4]
  _LinkVersion = 1
  _Parent = -> Elements007
FEATURE [App::FeaturePython] ElementLink094  label="_Element087"  # link proxy (typed FeaturePython)
  LinkTransform = true
  LinkedObject = -> _Element087
  _LinkVersion = 1
  _Parent = -> Constraint051
FEATURE [Part::FeaturePython] _Element087  # link proxy (typed FeaturePython)
  Detach = false
  LinkTransform = true
  LinkedObject = -> Link013 [Fillet001.Edge19]
  _LinkVersion = 1
  _Parent = -> Elements007
FEATURE [App::FeaturePython] Constraint052  label="Attachment043"  # WARN: FeaturePython — macro-defined, semantics opaque (R4)
  Cascade = false
  Disabled = false
  Group = -> [ElementLink095,ElementLink096]
  Multiply = false
  _ConstraintType = 45
  _LinkVersion = 1
  _Parent = -> Constraints007
FEATURE [App::FeaturePython] ElementLink095  label="_Element088"  # link proxy (typed FeaturePython)
  LinkTransform = true
  LinkedObject = -> _Element088
  Offset = pos=(0,0,0) rot=(1,0,0;3.14159rad)
  Placement = pos=(1.42e-14,-5.44e-14,-76.2) rot=(1,0,0;3.14159rad)
  _LinkVersion = 1
  _Parent = -> Constraint052
FEATURE [Part::FeaturePython] _Element088  # link proxy (typed FeaturePython)
  Detach = false
  LinkTransform = true
  LinkedObject = -> Link015 [1.Edge4]
  _LinkVersion = 1
  _Parent = -> Elements007
FEATURE [App::FeaturePython] ElementLink096  label="_Element089"  # link proxy (typed FeaturePython)
  LinkTransform = true
  LinkedObject = -> _Element089
  _LinkVersion = 1
  _Parent = -> Constraint052
FEATURE [Part::FeaturePython] _Element089  # link proxy (typed FeaturePython)
  Detach = false
  LinkTransform = true
  LinkedObject = -> Link013 [Fillet001.Edge16]
  _LinkVersion = 1
  _Parent = -> Elements007
FEATURE [Part::FeaturePython] Element008  label="beam mate"  # link proxy (typed FeaturePython)
  Detach = false
  LinkTransform = true
  LinkedObject = -> Link014 [Fillet001.Edge14]
  _LinkVersion = 1
  _Parent = -> Elements006
FEATURE [Part::FeaturePython] Element009  label="beam mate"  # link proxy (typed FeaturePython)
  Detach = false
  LinkTransform = true
  LinkedObject = -> Link013 [Fillet001.Edge31]
  _LinkVersion = 1
  _Parent = -> Elements007
FEATURE [Part::FeaturePython] Element010  label="limit mate"  # link proxy (typed FeaturePython)
  Detach = false
  LinkTransform = true
  LinkedObject = -> Link004 [Pocket.Edge16]
  _LinkVersion = 1
  _Parent = -> Elements004
FEATURE [Part::FeaturePython] Element011  label="limit mate"  # link proxy (typed FeaturePython)
  Detach = false
  LinkTransform = true
  LinkedObject = -> Link006 [Pocket.Edge41]
  _LinkVersion = 1
  _Parent = -> Elements005
